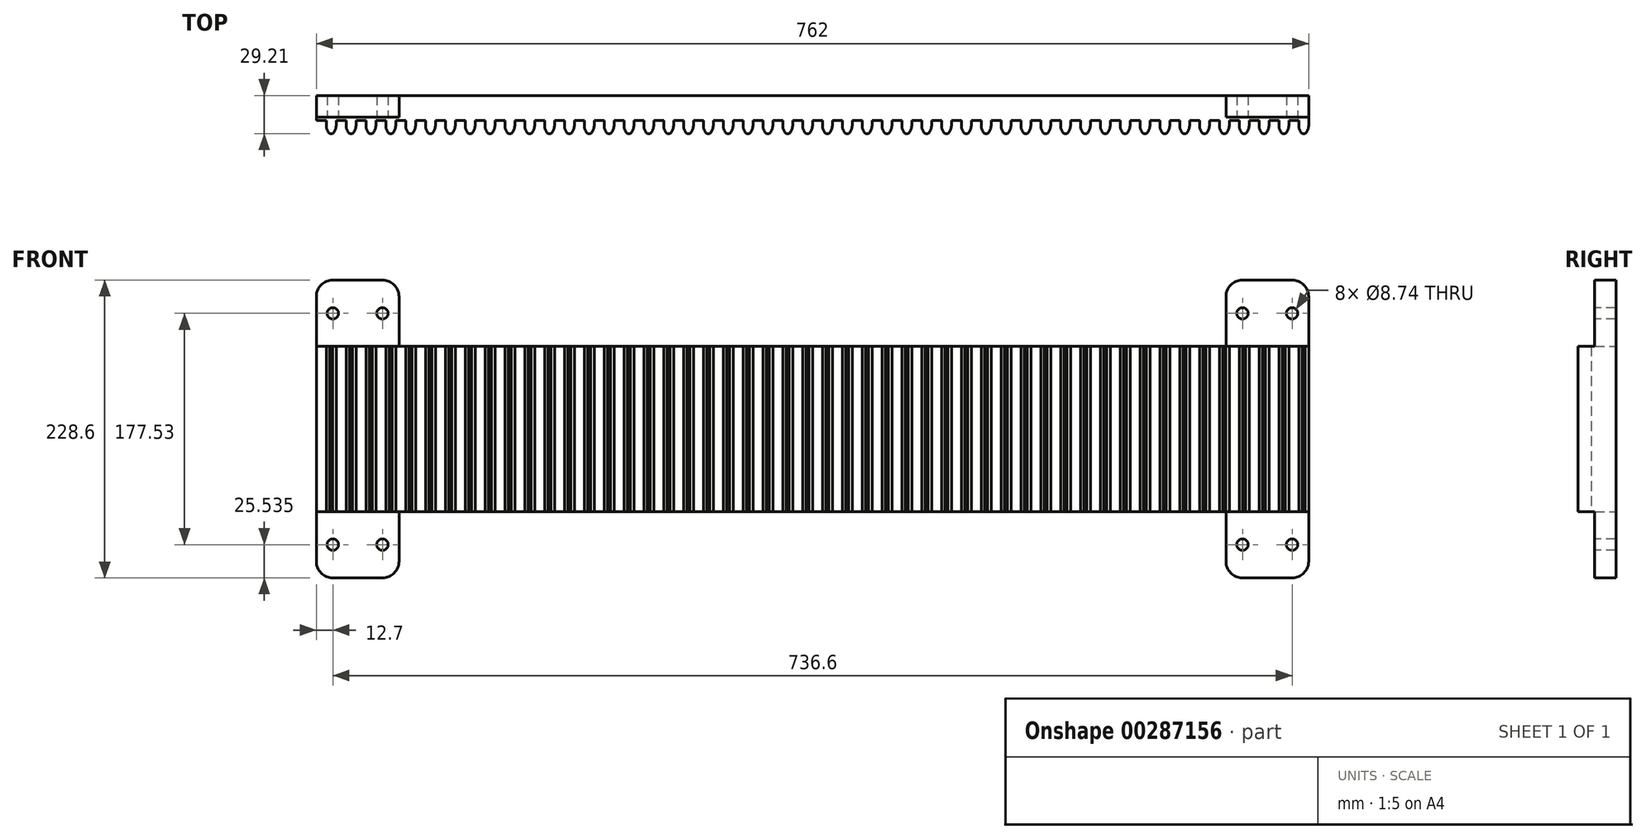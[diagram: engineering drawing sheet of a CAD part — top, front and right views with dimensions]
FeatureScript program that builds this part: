
annotation { "Feature Type Name" : "Feature", "Feature Type Description" : "" }
export const myFeature = defineFeature(function(context is Context, id is Id, definition is map)
    precondition{}
    {
        {
            var Q0;
            Q0=qCreatedBy(makeId("Front.planeOp"),FACE);
            var sketch = newSketch(context, id + "F0", { "sketchPlane" : qUnion([Q0])});
            skLineSegment(sketch, "E0", {"start": v(0, 0) * mm, "end": v(63.5, 0) * mm});
            skLineSegment(sketch, "E1.0", {"start": v(0, 228.6) * mm, "end": v(63.5, 228.6) * mm});
            skLineSegment(sketch, "E2", {"start": v(762, 0) * mm, "end": v(762, 228.6) * mm});
            skLineSegment(sketch, "E3", {"start": v(0, 228.6) * mm, "end": v(0, 0) * mm});
            skLineSegment(sketch, "E4.0", {"start": v(63.5, 177.8) * mm, "end": v(698.5, 177.8) * mm});
            skLineSegment(sketch, "E5.0", {"start": v(63.5, 50.8) * mm, "end": v(698.5, 50.8) * mm});
            skLineSegment(sketch, "E6.0", {"start": v(63.5, 228.6) * mm, "end": v(63.5, 177.8) * mm});
            skLineSegment(sketch, "E7.0", {"start": v(698.5, 0) * mm, "end": v(698.5, 50.8) * mm});
            skLineSegment(sketch, "E8.trimOffspring", {"start": v(698.5, 228.6) * mm, "end": v(762, 228.6) * mm});
            skLineSegment(sketch, "E9.trimOffspring", {"start": v(698.5, 0) * mm, "end": v(762, 0) * mm});
            skLineSegment(sketch, "E10.trimOffspring", {"start": v(698.5, 177.8) * mm, "end": v(698.5, 228.6) * mm});
            skLineSegment(sketch, "E11.trimOffspring", {"start": v(63.5, 50.8) * mm, "end": v(63.5, 0) * mm});
            skSolve(sketch);
        }
        {
            var Q0;
            Q0=qSketchRegion(id+"F0",true);
            extrude(context, id + "F1", {"entities" : qUnion([Q0]), "depth" : 19.05 * mm});
        }
        {
            var Q0;
            Q0=makeQuery(id+"F1.opExtrude","CAP_FACE",FACE,{"disambiguationData":[OSD([sQuery(id+"F0.wireOp",EDGE,"E0"),sQuery(id+"F0.wireOp",EDGE,"E1.0"),sQuery(id+"F0.wireOp",EDGE,"E2"),sQuery(id+"F0.wireOp",EDGE,"E3"),sQuery(id+"F0.wireOp",EDGE,"E4.0"),sQuery(id+"F0.wireOp",EDGE,"E5.0"),sQuery(id+"F0.wireOp",EDGE,"E6.0"),sQuery(id+"F0.wireOp",EDGE,"E7.0"),sQuery(id+"F0.wireOp",EDGE,"E8.trimOffspring"),sQuery(id+"F0.wireOp",EDGE,"E9.trimOffspring"),sQuery(id+"F0.wireOp",EDGE,"E10.trimOffspring"),sQuery(id+"F0.wireOp",EDGE,"E11.trimOffspring")])],"isStart":false});
            var sketch = newSketch(context, id + "F2", { "sketchPlane" : qUnion([Q0])});
            skLineSegment(sketch, "E12", {"start": v(762, 177.8) * mm, "end": v(0, 177.8) * mm});
            skLineSegment(sketch, "E13", {"start": v(0, 177.8) * mm, "end": v(0, 50.8) * mm});
            skLineSegment(sketch, "E14", {"start": v(0, 50.8) * mm, "end": v(762, 50.8) * mm});
            skLineSegment(sketch, "E15", {"start": v(762, 50.8) * mm, "end": v(762, 177.8) * mm});
            skLineSegment(sketch, "E16.1.0.0", {"start": v(7.62, 177.8) * mm, "end": v(7.62, 50.8) * mm});
            skLineSegment(sketch, "E16.2.0.0", {"start": v(15.24, 177.8) * mm, "end": v(15.24, 50.8) * mm});
            skLineSegment(sketch, "E16.direction1", {"start": v(0, 50.8) * mm, "end": v(7.62, 50.8) * mm, "construction": true});
            skLineSegment(sketch, "E17.0.3.0", {"start": v(22.86, 177.8) * mm, "end": v(22.86, 50.8) * mm});
            skLineSegment(sketch, "E17.0.4.0", {"start": v(30.48, 177.8) * mm, "end": v(30.48, 50.8) * mm});
            skLineSegment(sketch, "E17.0.5.0", {"start": v(38.1, 177.8) * mm, "end": v(38.1, 50.8) * mm});
            skLineSegment(sketch, "E17.0.6.0", {"start": v(45.72, 177.8) * mm, "end": v(45.72, 50.8) * mm});
            skLineSegment(sketch, "E17.0.7.0", {"start": v(53.34, 177.8) * mm, "end": v(53.34, 50.8) * mm});
            skLineSegment(sketch, "E17.0.8.0", {"start": v(60.96, 177.8) * mm, "end": v(60.96, 50.8) * mm});
            skLineSegment(sketch, "E17.0.9.0", {"start": v(68.58, 177.8) * mm, "end": v(68.58, 50.8) * mm});
            skLineSegment(sketch, "E17.0.10.0", {"start": v(76.2, 177.8) * mm, "end": v(76.2, 50.8) * mm});
            skLineSegment(sketch, "E17.0.11.0", {"start": v(83.82, 177.8) * mm, "end": v(83.82, 50.8) * mm});
            skLineSegment(sketch, "E17.0.12.0", {"start": v(91.44, 177.8) * mm, "end": v(91.44, 50.8) * mm});
            skLineSegment(sketch, "E17.0.13.0", {"start": v(99.06, 177.8) * mm, "end": v(99.06, 50.8) * mm});
            skLineSegment(sketch, "E17.0.14.0", {"start": v(106.68, 177.8) * mm, "end": v(106.68, 50.8) * mm});
            skLineSegment(sketch, "E17.0.15.0", {"start": v(114.3, 177.8) * mm, "end": v(114.3, 50.8) * mm});
            skLineSegment(sketch, "E17.0.16.0", {"start": v(121.92, 177.8) * mm, "end": v(121.92, 50.8) * mm});
            skLineSegment(sketch, "E17.0.17.0", {"start": v(129.54, 177.8) * mm, "end": v(129.54, 50.8) * mm});
            skLineSegment(sketch, "E17.0.18.0", {"start": v(137.16, 177.8) * mm, "end": v(137.16, 50.8) * mm});
            skLineSegment(sketch, "E17.0.19.0", {"start": v(144.78, 177.8) * mm, "end": v(144.78, 50.8) * mm});
            skLineSegment(sketch, "E17.0.20.0", {"start": v(152.4, 177.8) * mm, "end": v(152.4, 50.8) * mm});
            skLineSegment(sketch, "E17.0.21.0", {"start": v(160.02, 177.8) * mm, "end": v(160.02, 50.8) * mm});
            skLineSegment(sketch, "E17.0.22.0", {"start": v(167.64, 177.8) * mm, "end": v(167.64, 50.8) * mm});
            skLineSegment(sketch, "E17.0.23.0", {"start": v(175.26, 177.8) * mm, "end": v(175.26, 50.8) * mm});
            skLineSegment(sketch, "E17.0.24.0", {"start": v(182.88, 177.8) * mm, "end": v(182.88, 50.8) * mm});
            skLineSegment(sketch, "E17.0.25.0", {"start": v(190.5, 177.8) * mm, "end": v(190.5, 50.8) * mm});
            skLineSegment(sketch, "E17.0.26.0", {"start": v(198.12, 177.8) * mm, "end": v(198.12, 50.8) * mm});
            skLineSegment(sketch, "E17.0.27.0", {"start": v(205.74, 177.8) * mm, "end": v(205.74, 50.8) * mm});
            skLineSegment(sketch, "E17.0.28.0", {"start": v(213.36, 177.8) * mm, "end": v(213.36, 50.8) * mm});
            skLineSegment(sketch, "E17.0.29.0", {"start": v(220.98, 177.8) * mm, "end": v(220.98, 50.8) * mm});
            skLineSegment(sketch, "E17.0.30.0", {"start": v(228.6, 177.8) * mm, "end": v(228.6, 50.8) * mm});
            skLineSegment(sketch, "E17.0.31.0", {"start": v(236.22, 177.8) * mm, "end": v(236.22, 50.8) * mm});
            skLineSegment(sketch, "E17.0.32.0", {"start": v(243.84, 177.8) * mm, "end": v(243.84, 50.8) * mm});
            skLineSegment(sketch, "E17.0.33.0", {"start": v(251.46, 177.8) * mm, "end": v(251.46, 50.8) * mm});
            skLineSegment(sketch, "E17.0.34.0", {"start": v(259.08, 177.8) * mm, "end": v(259.08, 50.8) * mm});
            skLineSegment(sketch, "E17.0.35.0", {"start": v(266.7, 177.8) * mm, "end": v(266.7, 50.8) * mm});
            skLineSegment(sketch, "E17.0.36.0", {"start": v(274.32, 177.8) * mm, "end": v(274.32, 50.8) * mm});
            skLineSegment(sketch, "E17.0.37.0", {"start": v(281.94, 177.8) * mm, "end": v(281.94, 50.8) * mm});
            skLineSegment(sketch, "E17.0.38.0", {"start": v(289.56, 177.8) * mm, "end": v(289.56, 50.8) * mm});
            skLineSegment(sketch, "E17.0.39.0", {"start": v(297.18, 177.8) * mm, "end": v(297.18, 50.8) * mm});
            skLineSegment(sketch, "E17.0.40.0", {"start": v(304.8, 177.8) * mm, "end": v(304.8, 50.8) * mm});
            skLineSegment(sketch, "E17.0.41.0", {"start": v(312.42, 177.8) * mm, "end": v(312.42, 50.8) * mm});
            skLineSegment(sketch, "E17.0.42.0", {"start": v(320.04, 177.8) * mm, "end": v(320.04, 50.8) * mm});
            skLineSegment(sketch, "E17.0.43.0", {"start": v(327.66, 177.8) * mm, "end": v(327.66, 50.8) * mm});
            skLineSegment(sketch, "E17.0.44.0", {"start": v(335.28, 177.8) * mm, "end": v(335.28, 50.8) * mm});
            skLineSegment(sketch, "E17.0.45.0", {"start": v(342.9, 177.8) * mm, "end": v(342.9, 50.8) * mm});
            skLineSegment(sketch, "E17.0.46.0", {"start": v(350.52, 177.8) * mm, "end": v(350.52, 50.8) * mm});
            skLineSegment(sketch, "E17.0.47.0", {"start": v(358.14, 177.8) * mm, "end": v(358.14, 50.8) * mm});
            skLineSegment(sketch, "E17.0.48.0", {"start": v(365.76, 177.8) * mm, "end": v(365.76, 50.8) * mm});
            skLineSegment(sketch, "E17.0.49.0", {"start": v(373.38, 177.8) * mm, "end": v(373.38, 50.8) * mm});
            skLineSegment(sketch, "E18.0.50.0", {"start": v(381, 177.8) * mm, "end": v(381, 50.8) * mm});
            skLineSegment(sketch, "E18.0.51.0", {"start": v(388.62, 177.8) * mm, "end": v(388.62, 50.8) * mm});
            skLineSegment(sketch, "E18.0.52.0", {"start": v(396.24, 177.8) * mm, "end": v(396.24, 50.8) * mm});
            skLineSegment(sketch, "E18.0.53.0", {"start": v(403.86, 177.8) * mm, "end": v(403.86, 50.8) * mm});
            skLineSegment(sketch, "E18.0.54.0", {"start": v(411.48, 177.8) * mm, "end": v(411.48, 50.8) * mm});
            skLineSegment(sketch, "E18.0.55.0", {"start": v(419.1, 177.8) * mm, "end": v(419.1, 50.8) * mm});
            skLineSegment(sketch, "E18.0.56.0", {"start": v(426.72, 177.8) * mm, "end": v(426.72, 50.8) * mm});
            skLineSegment(sketch, "E18.0.57.0", {"start": v(434.34, 177.8) * mm, "end": v(434.34, 50.8) * mm});
            skLineSegment(sketch, "E18.0.58.0", {"start": v(441.96, 177.8) * mm, "end": v(441.96, 50.8) * mm});
            skLineSegment(sketch, "E18.0.59.0", {"start": v(449.58, 177.8) * mm, "end": v(449.58, 50.8) * mm});
            skLineSegment(sketch, "E18.0.60.0", {"start": v(457.2, 177.8) * mm, "end": v(457.2, 50.8) * mm});
            skLineSegment(sketch, "E18.0.61.0", {"start": v(464.82, 177.8) * mm, "end": v(464.82, 50.8) * mm});
            skLineSegment(sketch, "E18.0.62.0", {"start": v(472.44, 177.8) * mm, "end": v(472.44, 50.8) * mm});
            skLineSegment(sketch, "E18.0.63.0", {"start": v(480.06, 177.8) * mm, "end": v(480.06, 50.8) * mm});
            skLineSegment(sketch, "E18.0.64.0", {"start": v(487.68, 177.8) * mm, "end": v(487.68, 50.8) * mm});
            skLineSegment(sketch, "E18.0.65.0", {"start": v(495.3, 177.8) * mm, "end": v(495.3, 50.8) * mm});
            skLineSegment(sketch, "E18.0.66.0", {"start": v(502.92, 177.8) * mm, "end": v(502.92, 50.8) * mm});
            skLineSegment(sketch, "E18.0.67.0", {"start": v(510.54, 177.8) * mm, "end": v(510.54, 50.8) * mm});
            skLineSegment(sketch, "E18.0.68.0", {"start": v(518.16, 177.8) * mm, "end": v(518.16, 50.8) * mm});
            skLineSegment(sketch, "E18.0.69.0", {"start": v(525.78, 177.8) * mm, "end": v(525.78, 50.8) * mm});
            skLineSegment(sketch, "E18.0.70.0", {"start": v(533.4, 177.8) * mm, "end": v(533.4, 50.8) * mm});
            skLineSegment(sketch, "E18.0.71.0", {"start": v(541.02, 177.8) * mm, "end": v(541.02, 50.8) * mm});
            skLineSegment(sketch, "E18.0.72.0", {"start": v(548.64, 177.8) * mm, "end": v(548.64, 50.8) * mm});
            skLineSegment(sketch, "E18.0.73.0", {"start": v(556.26, 177.8) * mm, "end": v(556.26, 50.8) * mm});
            skLineSegment(sketch, "E18.0.74.0", {"start": v(563.88, 177.8) * mm, "end": v(563.88, 50.8) * mm});
            skLineSegment(sketch, "E18.0.75.0", {"start": v(571.5, 177.8) * mm, "end": v(571.5, 50.8) * mm});
            skLineSegment(sketch, "E18.0.76.0", {"start": v(579.12, 177.8) * mm, "end": v(579.12, 50.8) * mm});
            skLineSegment(sketch, "E18.0.77.0", {"start": v(586.74, 177.8) * mm, "end": v(586.74, 50.8) * mm});
            skLineSegment(sketch, "E18.0.78.0", {"start": v(594.36, 177.8) * mm, "end": v(594.36, 50.8) * mm});
            skLineSegment(sketch, "E18.0.79.0", {"start": v(601.98, 177.8) * mm, "end": v(601.98, 50.8) * mm});
            skLineSegment(sketch, "E18.0.80.0", {"start": v(609.6, 177.8) * mm, "end": v(609.6, 50.8) * mm});
            skLineSegment(sketch, "E18.0.81.0", {"start": v(617.22, 177.8) * mm, "end": v(617.22, 50.8) * mm});
            skLineSegment(sketch, "E18.0.82.0", {"start": v(624.84, 177.8) * mm, "end": v(624.84, 50.8) * mm});
            skLineSegment(sketch, "E18.0.83.0", {"start": v(632.46, 177.8) * mm, "end": v(632.46, 50.8) * mm});
            skLineSegment(sketch, "E18.0.84.0", {"start": v(640.08, 177.8) * mm, "end": v(640.08, 50.8) * mm});
            skLineSegment(sketch, "E18.0.85.0", {"start": v(647.7, 177.8) * mm, "end": v(647.7, 50.8) * mm});
            skLineSegment(sketch, "E18.0.86.0", {"start": v(655.32, 177.8) * mm, "end": v(655.32, 50.8) * mm});
            skLineSegment(sketch, "E18.0.87.0", {"start": v(662.94, 177.8) * mm, "end": v(662.94, 50.8) * mm});
            skLineSegment(sketch, "E18.0.88.0", {"start": v(670.56, 177.8) * mm, "end": v(670.56, 50.8) * mm});
            skLineSegment(sketch, "E18.0.89.0", {"start": v(678.18, 177.8) * mm, "end": v(678.18, 50.8) * mm});
            skLineSegment(sketch, "E18.0.90.0", {"start": v(685.8, 177.8) * mm, "end": v(685.8, 50.8) * mm});
            skLineSegment(sketch, "E18.0.91.0", {"start": v(693.42, 177.8) * mm, "end": v(693.42, 50.8) * mm});
            skLineSegment(sketch, "E18.0.92.0", {"start": v(701.04, 177.8) * mm, "end": v(701.04, 50.8) * mm});
            skLineSegment(sketch, "E18.0.93.0", {"start": v(708.66, 177.8) * mm, "end": v(708.66, 50.8) * mm});
            skLineSegment(sketch, "E18.0.94.0", {"start": v(716.28, 177.8) * mm, "end": v(716.28, 50.8) * mm});
            skLineSegment(sketch, "E18.0.95.0", {"start": v(723.9, 177.8) * mm, "end": v(723.9, 50.8) * mm});
            skLineSegment(sketch, "E18.0.96.0", {"start": v(731.52, 177.8) * mm, "end": v(731.52, 50.8) * mm});
            skLineSegment(sketch, "E18.0.97.0", {"start": v(739.14, 177.8) * mm, "end": v(739.14, 50.8) * mm});
            skLineSegment(sketch, "E18.0.98.0", {"start": v(746.76, 177.8) * mm, "end": v(746.76, 50.8) * mm});
            skLineSegment(sketch, "E18.0.99.0", {"start": v(754.38, 177.8) * mm, "end": v(754.38, 50.8) * mm});
            skSolve(sketch);
        }
        {
            var Q0;
            {var subQ7=makeQuery(id+"F1.opExtrude","CAP_EDGE",EDGE,{"disambiguationData":[OSD([sQuery(id+"F0.wireOp",EDGE,"E1.0")])],"isStart":false});Q0=makeQuery(id+"F2.imprint","IMPRINT",FACE,{"disambiguationData":[TD([[makeQuery(id+"F2.imprint","IMPRINT",EDGE,{"derivedFrom":subQ7}),-1.0]])]});}
            var sketch = newSketch(context, id + "F3", { "sketchPlane" : qUnion([Q0])});
            skLineSegment(sketch, "E19", {"start": v(0, 228.6) * mm, "end": v(63.5, 228.6) * mm});
            skLineSegment(sketch, "E20", {"start": v(63.5, 228.6) * mm, "end": v(63.5, 177.8) * mm});
            skLineSegment(sketch, "E21", {"start": v(63.5, 177.8) * mm, "end": v(0, 177.8) * mm});
            skLineSegment(sketch, "E22", {"start": v(0, 0) * mm, "end": v(0, 50.8) * mm});
            skLineSegment(sketch, "E23", {"start": v(0, 50.8) * mm, "end": v(63.5, 50.8) * mm});
            skLineSegment(sketch, "E24", {"start": v(63.5, 50.8) * mm, "end": v(63.5, 0) * mm});
            skLineSegment(sketch, "E25", {"start": v(63.5, 0) * mm, "end": v(0, 0) * mm});
            skSolve(sketch);
        }
        {
            var Q0;
            Q0=qSketchRegion(id+"F3",true);
            var Q1;
            {var subQ8=sQuery(id+"F3.wireOp",EDGE,"E19");Q1=makeQuery(id+"F3.imprint","IMPRINT",FACE,{"disambiguationData":[TD([[makeQuery(id+"F3.imprint","IMPRINT",EDGE,{"derivedFrom":subQ8}),-1.0]])]});}
            extrude(context, id + "F4", {"entities" : qUnion([Q0, Q1]), "operationType" : NewBodyOperationType.REMOVE, "oppositeDirection" : true, "depth" : 2.54 * mm});
        }
        {
            var Q0;
            {var subQ1=sQuery(id+"F0.wireOp",EDGE,"E7.0");var subQ7=sQuery(id+"F0.wireOp",EDGE,"E8.trimOffspring");var subQ10=sQuery(id+"F0.wireOp",EDGE,"E9.trimOffspring");var subQ50=sQuery(id+"F0.wireOp",EDGE,"E4.0");var subQ83=sQuery(id+"F0.wireOp",EDGE,"E10.trimOffspring");var subQ89=sQuery(id+"F0.wireOp",EDGE,"E2");var subQ94=sQuery(id+"F0.wireOp",EDGE,"E5.0");Q0=makeQuery(id+"F9L2YdqkWQCteiL_1.boolean.opBoolean","SPLIT",FACE,{"disambiguationData":[TD([makeQuery(id+"F1.opExtrude","SWEPT_FACE",FACE,{"disambiguationData":[OSD([subQ89])]})])],"derivedFrom":makeQuery(id+"F1.opExtrude","CAP_FACE",FACE,{"disambiguationData":[OSD([sQuery(id+"F0.wireOp",EDGE,"E0"),sQuery(id+"F0.wireOp",EDGE,"E1.0"),subQ89,sQuery(id+"F0.wireOp",EDGE,"E3"),subQ50,subQ94,sQuery(id+"F0.wireOp",EDGE,"E6.0"),subQ1,subQ7,subQ10,subQ83,sQuery(id+"F0.wireOp",EDGE,"E11.trimOffspring")])],"isStart":false})});}
            var sketch = newSketch(context, id + "F5", { "sketchPlane" : qUnion([Q0])});
            skLineSegment(sketch, "E26", {"start": v(698.5, 228.6) * mm, "end": v(698.5, 177.8) * mm});
            skLineSegment(sketch, "E27", {"start": v(698.5, 177.8) * mm, "end": v(762, 177.8) * mm});
            skLineSegment(sketch, "E28", {"start": v(762, 177.8) * mm, "end": v(762, 228.6) * mm});
            skLineSegment(sketch, "E29", {"start": v(762, 228.6) * mm, "end": v(698.5, 228.6) * mm});
            skLineSegment(sketch, "E30", {"start": v(698.5, 0) * mm, "end": v(762, 0) * mm});
            skLineSegment(sketch, "E31", {"start": v(762, 0) * mm, "end": v(762, 50.8) * mm});
            skLineSegment(sketch, "E32", {"start": v(762, 50.8) * mm, "end": v(701.04, 50.8) * mm});
            skLineSegment(sketch, "E33", {"start": v(701.04, 50.8) * mm, "end": v(698.5, 50.8) * mm});
            skLineSegment(sketch, "E34", {"start": v(698.5, 50.8) * mm, "end": v(698.5, 0) * mm});
            skSolve(sketch);
        }
        {
            var Q0;
            {var subQ7=sQuery(id+"F5.wireOp",EDGE,"E26");Q0=makeQuery(id+"F5.imprint","IMPRINT",FACE,{"disambiguationData":[TD([[makeQuery(id+"F5.imprint","IMPRINT",EDGE,{"derivedFrom":subQ7}),-1.0]])]});}
            var Q1;
            Q1=makeQuery(id+"F5.imprint","IMPRINT",FACE,{"disambiguationData":[TD([[makeQuery(id+"F5.imprint","IMPRINT",EDGE,{"derivedFrom":sQuery(id+"F5.wireOp",EDGE,"E30")}),1.0]])]});
            extrude(context, id + "F6", {"entities" : qUnion([Q0, Q1]), "operationType" : NewBodyOperationType.REMOVE, "oppositeDirection" : true, "depth" : 2.54 * mm});
        }
        {
            var Q0;
            Q0=makeQuery(id+"F1.opExtrude","SWEPT_EDGE",EDGE,{"disambiguationData":[OSD([sQuery(id+"F0.wireOp",EDGE,"E1.0"),sQuery(id+"F0.wireOp",EDGE,"E6.0")])]});
            var Q1;
            Q1=makeQuery(id+"F1.opExtrude","SWEPT_EDGE",EDGE,{"disambiguationData":[OSD([sQuery(id+"F0.wireOp",EDGE,"E1.0"),sQuery(id+"F0.wireOp",EDGE,"E3")])]});
            var Q2;
            Q2=makeQuery(id+"F1.opExtrude","SWEPT_EDGE",EDGE,{"disambiguationData":[OSD([sQuery(id+"F0.wireOp",EDGE,"E0"),sQuery(id+"F0.wireOp",EDGE,"E11.trimOffspring")])]});
            var Q3;
            Q3=makeQuery(id+"F1.opExtrude","SWEPT_EDGE",EDGE,{"disambiguationData":[OSD([sQuery(id+"F0.wireOp",EDGE,"E0"),sQuery(id+"F0.wireOp",EDGE,"E3")])]});
            var Q4;
            Q4=makeQuery(id+"F1.opExtrude","SWEPT_EDGE",EDGE,{"disambiguationData":[OSD([sQuery(id+"F0.wireOp",EDGE,"E2"),sQuery(id+"F0.wireOp",EDGE,"E8.trimOffspring")])]});
            var Q5;
            Q5=makeQuery(id+"F1.opExtrude","SWEPT_EDGE",EDGE,{"disambiguationData":[OSD([sQuery(id+"F0.wireOp",EDGE,"E8.trimOffspring"),sQuery(id+"F0.wireOp",EDGE,"E10.trimOffspring")])]});
            var Q6;
            Q6=makeQuery(id+"F1.opExtrude","SWEPT_EDGE",EDGE,{"disambiguationData":[OSD([sQuery(id+"F0.wireOp",EDGE,"E2"),sQuery(id+"F0.wireOp",EDGE,"E9.trimOffspring")])]});
            var Q7;
            Q7=makeQuery(id+"F1.opExtrude","SWEPT_EDGE",EDGE,{"disambiguationData":[OSD([sQuery(id+"F0.wireOp",EDGE,"E7.0"),sQuery(id+"F0.wireOp",EDGE,"E9.trimOffspring")])]});
            fillet(context, id + "F7", {"entities" : qUnion([Q0, Q1, Q2, Q3, Q4, Q5, Q6, Q7]), "radius" : 12.7 * mm, "tangentPropagation" : true, "allowEdgeOverflow" : false});
        }
        {
            var Q0;
            {var subQ0=sQuery(id+"F2.wireOp",EDGE,"E14");var subQ1=makeQuery(id+"F2.imprint","INTERSECT",VERTEX,{"derivedFrom":[makeQuery(id+"F1.opExtrude","CAP_EDGE",EDGE,{"disambiguationData":[OSD([sQuery(id+"F0.wireOp",EDGE,"E7.0")])],"isStart":false}),subQ0]});Q0=makeQuery(id+"F6.boolean.opBoolean","MERGE",FACE,{"derivedFrom":[makeQuery(id+"F9L2YdqkWQCteiL_1.opExtrude","SWEPT_FACE",FACE,{"disambiguationData":[OSD([subQ0]),TDD([makeQuery(id+"F2.imprint","IMPRINT",EDGE,{"disambiguationData":[TD([[makeQuery(id+"F2.imprint","INTERSECT",VERTEX,{"derivedFrom":[subQ0,sQuery(id+"F2.wireOp",EDGE,"E18.0.93.0")]}),-1.0]])],"derivedFrom":subQ0})])]}),makeQuery(id+"F9L2YdqkWQCteiL_1.opExtrude","SWEPT_FACE",FACE,{"disambiguationData":[OSD([subQ0]),TDD([makeQuery(id+"F2.imprint","IMPRINT",EDGE,{"disambiguationData":[TD([[makeQuery(id+"F2.imprint","INTERSECT",VERTEX,{"derivedFrom":[subQ0,sQuery(id+"F2.wireOp",EDGE,"E18.0.95.0")]}),-1.0]])],"derivedFrom":subQ0})])]}),makeQuery(id+"F9L2YdqkWQCteiL_1.opExtrude","SWEPT_FACE",FACE,{"disambiguationData":[OSD([subQ0]),TDD([makeQuery(id+"F2.imprint","IMPRINT",EDGE,{"disambiguationData":[TD([[makeQuery(id+"F2.imprint","INTERSECT",VERTEX,{"derivedFrom":[subQ0,sQuery(id+"F2.wireOp",EDGE,"E18.0.97.0")]}),-1.0]])],"derivedFrom":subQ0})])]}),makeQuery(id+"F9L2YdqkWQCteiL_1.opExtrude","SWEPT_FACE",FACE,{"disambiguationData":[OSD([subQ0]),TDD([makeQuery(id+"F2.imprint","IMPRINT",EDGE,{"disambiguationData":[TD([[makeQuery(id+"F2.imprint","INTERSECT",VERTEX,{"derivedFrom":[subQ0,sQuery(id+"F2.wireOp",EDGE,"E18.0.99.0")]}),-1.0]])],"derivedFrom":subQ0})])]}),makeQuery(id+"F4.boolean.opBoolean","MERGE",FACE,{"derivedFrom":[makeQuery(id+"F9L2YdqkWQCteiL_1.opExtrude","SWEPT_FACE",FACE,{"disambiguationData":[OSD([subQ0]),TDD([makeQuery(id+"F2.imprint","IMPRINT",EDGE,{"disambiguationData":[TD([[makeQuery(id+"F2.imprint","INTERSECT",VERTEX,{"derivedFrom":[subQ0,sQuery(id+"F2.wireOp",EDGE,"E16.1.0.0")]}),-1.0]])],"derivedFrom":subQ0})])]}),makeQuery(id+"F9L2YdqkWQCteiL_1.opExtrude","SWEPT_FACE",FACE,{"disambiguationData":[OSD([subQ0]),TDD([makeQuery(id+"F2.imprint","IMPRINT",EDGE,{"disambiguationData":[TD([[makeQuery(id+"F2.imprint","INTERSECT",VERTEX,{"derivedFrom":[subQ0,sQuery(id+"F2.wireOp",EDGE,"E17.0.3.0")]}),-1.0]])],"derivedFrom":subQ0})])]}),makeQuery(id+"F9L2YdqkWQCteiL_1.opExtrude","SWEPT_FACE",FACE,{"disambiguationData":[OSD([subQ0]),TDD([makeQuery(id+"F2.imprint","IMPRINT",EDGE,{"disambiguationData":[TD([[makeQuery(id+"F2.imprint","INTERSECT",VERTEX,{"derivedFrom":[subQ0,sQuery(id+"F2.wireOp",EDGE,"E17.0.5.0")]}),-1.0]])],"derivedFrom":subQ0})])]}),makeQuery(id+"F9L2YdqkWQCteiL_1.opExtrude","SWEPT_FACE",FACE,{"disambiguationData":[OSD([subQ0]),TDD([makeQuery(id+"F2.imprint","IMPRINT",EDGE,{"disambiguationData":[TD([[makeQuery(id+"F2.imprint","INTERSECT",VERTEX,{"derivedFrom":[subQ0,sQuery(id+"F2.wireOp",EDGE,"E17.0.7.0")]}),-1.0]])],"derivedFrom":subQ0})])]}),makeQuery(id+"F9L2YdqkWQCteiL_1.boolean.opBoolean","MERGE",FACE,{"derivedFrom":[makeQuery(id+"F1.opExtrude","SWEPT_FACE",FACE,{"disambiguationData":[OSD([sQuery(id+"F0.wireOp",EDGE,"E5.0")])]}),makeQuery(id+"F9L2YdqkWQCteiL_1.opExtrude","SWEPT_FACE",FACE,{"disambiguationData":[OSD([subQ0]),TDD([makeQuery(id+"F2.imprint","IMPRINT",EDGE,{"disambiguationData":[TD([[makeQuery(id+"F2.imprint","INTERSECT",VERTEX,{"derivedFrom":[subQ0,sQuery(id+"F2.wireOp",EDGE,"E17.0.9.0")]}),-1.0]])],"derivedFrom":subQ0})])]}),makeQuery(id+"F9L2YdqkWQCteiL_1.opExtrude","SWEPT_FACE",FACE,{"disambiguationData":[OSD([subQ0]),TDD([makeQuery(id+"F2.imprint","IMPRINT",EDGE,{"disambiguationData":[TD([[makeQuery(id+"F2.imprint","INTERSECT",VERTEX,{"derivedFrom":[subQ0,sQuery(id+"F2.wireOp",EDGE,"E17.0.11.0")]}),-1.0]])],"derivedFrom":subQ0})])]}),makeQuery(id+"F9L2YdqkWQCteiL_1.opExtrude","SWEPT_FACE",FACE,{"disambiguationData":[OSD([subQ0]),TDD([makeQuery(id+"F2.imprint","IMPRINT",EDGE,{"disambiguationData":[TD([[makeQuery(id+"F2.imprint","INTERSECT",VERTEX,{"derivedFrom":[subQ0,sQuery(id+"F2.wireOp",EDGE,"E17.0.13.0")]}),-1.0]])],"derivedFrom":subQ0})])]}),makeQuery(id+"F9L2YdqkWQCteiL_1.opExtrude","SWEPT_FACE",FACE,{"disambiguationData":[OSD([subQ0]),TDD([makeQuery(id+"F2.imprint","IMPRINT",EDGE,{"disambiguationData":[TD([[makeQuery(id+"F2.imprint","INTERSECT",VERTEX,{"derivedFrom":[subQ0,sQuery(id+"F2.wireOp",EDGE,"E17.0.15.0")]}),-1.0]])],"derivedFrom":subQ0})])]}),makeQuery(id+"F9L2YdqkWQCteiL_1.opExtrude","SWEPT_FACE",FACE,{"disambiguationData":[OSD([subQ0]),TDD([makeQuery(id+"F2.imprint","IMPRINT",EDGE,{"disambiguationData":[TD([[makeQuery(id+"F2.imprint","INTERSECT",VERTEX,{"derivedFrom":[subQ0,sQuery(id+"F2.wireOp",EDGE,"E17.0.17.0")]}),-1.0]])],"derivedFrom":subQ0})])]}),makeQuery(id+"F9L2YdqkWQCteiL_1.opExtrude","SWEPT_FACE",FACE,{"disambiguationData":[OSD([subQ0]),TDD([makeQuery(id+"F2.imprint","IMPRINT",EDGE,{"disambiguationData":[TD([[makeQuery(id+"F2.imprint","INTERSECT",VERTEX,{"derivedFrom":[subQ0,sQuery(id+"F2.wireOp",EDGE,"E17.0.19.0")]}),-1.0]])],"derivedFrom":subQ0})])]}),makeQuery(id+"F9L2YdqkWQCteiL_1.opExtrude","SWEPT_FACE",FACE,{"disambiguationData":[OSD([subQ0]),TDD([makeQuery(id+"F2.imprint","IMPRINT",EDGE,{"disambiguationData":[TD([[makeQuery(id+"F2.imprint","INTERSECT",VERTEX,{"derivedFrom":[subQ0,sQuery(id+"F2.wireOp",EDGE,"E17.0.21.0")]}),-1.0]])],"derivedFrom":subQ0})])]}),makeQuery(id+"F9L2YdqkWQCteiL_1.opExtrude","SWEPT_FACE",FACE,{"disambiguationData":[OSD([subQ0]),TDD([makeQuery(id+"F2.imprint","IMPRINT",EDGE,{"disambiguationData":[TD([[makeQuery(id+"F2.imprint","INTERSECT",VERTEX,{"derivedFrom":[subQ0,sQuery(id+"F2.wireOp",EDGE,"E17.0.23.0")]}),-1.0]])],"derivedFrom":subQ0})])]}),makeQuery(id+"F9L2YdqkWQCteiL_1.opExtrude","SWEPT_FACE",FACE,{"disambiguationData":[OSD([subQ0]),TDD([makeQuery(id+"F2.imprint","IMPRINT",EDGE,{"disambiguationData":[TD([[makeQuery(id+"F2.imprint","INTERSECT",VERTEX,{"derivedFrom":[subQ0,sQuery(id+"F2.wireOp",EDGE,"E17.0.25.0")]}),-1.0]])],"derivedFrom":subQ0})])]}),makeQuery(id+"F9L2YdqkWQCteiL_1.opExtrude","SWEPT_FACE",FACE,{"disambiguationData":[OSD([subQ0]),TDD([makeQuery(id+"F2.imprint","IMPRINT",EDGE,{"disambiguationData":[TD([[makeQuery(id+"F2.imprint","INTERSECT",VERTEX,{"derivedFrom":[subQ0,sQuery(id+"F2.wireOp",EDGE,"E17.0.27.0")]}),-1.0]])],"derivedFrom":subQ0})])]}),makeQuery(id+"F9L2YdqkWQCteiL_1.opExtrude","SWEPT_FACE",FACE,{"disambiguationData":[OSD([subQ0]),TDD([makeQuery(id+"F2.imprint","IMPRINT",EDGE,{"disambiguationData":[TD([[makeQuery(id+"F2.imprint","INTERSECT",VERTEX,{"derivedFrom":[subQ0,sQuery(id+"F2.wireOp",EDGE,"E17.0.29.0")]}),-1.0]])],"derivedFrom":subQ0})])]}),makeQuery(id+"F9L2YdqkWQCteiL_1.opExtrude","SWEPT_FACE",FACE,{"disambiguationData":[OSD([subQ0]),TDD([makeQuery(id+"F2.imprint","IMPRINT",EDGE,{"disambiguationData":[TD([[makeQuery(id+"F2.imprint","INTERSECT",VERTEX,{"derivedFrom":[subQ0,sQuery(id+"F2.wireOp",EDGE,"E17.0.31.0")]}),-1.0]])],"derivedFrom":subQ0})])]}),makeQuery(id+"F9L2YdqkWQCteiL_1.opExtrude","SWEPT_FACE",FACE,{"disambiguationData":[OSD([subQ0]),TDD([makeQuery(id+"F2.imprint","IMPRINT",EDGE,{"disambiguationData":[TD([[makeQuery(id+"F2.imprint","INTERSECT",VERTEX,{"derivedFrom":[subQ0,sQuery(id+"F2.wireOp",EDGE,"E17.0.33.0")]}),-1.0]])],"derivedFrom":subQ0})])]}),makeQuery(id+"F9L2YdqkWQCteiL_1.opExtrude","SWEPT_FACE",FACE,{"disambiguationData":[OSD([subQ0]),TDD([makeQuery(id+"F2.imprint","IMPRINT",EDGE,{"disambiguationData":[TD([[makeQuery(id+"F2.imprint","INTERSECT",VERTEX,{"derivedFrom":[subQ0,sQuery(id+"F2.wireOp",EDGE,"E17.0.35.0")]}),-1.0]])],"derivedFrom":subQ0})])]}),makeQuery(id+"F9L2YdqkWQCteiL_1.opExtrude","SWEPT_FACE",FACE,{"disambiguationData":[OSD([subQ0]),TDD([makeQuery(id+"F2.imprint","IMPRINT",EDGE,{"disambiguationData":[TD([[makeQuery(id+"F2.imprint","INTERSECT",VERTEX,{"derivedFrom":[subQ0,sQuery(id+"F2.wireOp",EDGE,"E17.0.37.0")]}),-1.0]])],"derivedFrom":subQ0})])]}),makeQuery(id+"F9L2YdqkWQCteiL_1.opExtrude","SWEPT_FACE",FACE,{"disambiguationData":[OSD([subQ0]),TDD([makeQuery(id+"F2.imprint","IMPRINT",EDGE,{"disambiguationData":[TD([[makeQuery(id+"F2.imprint","INTERSECT",VERTEX,{"derivedFrom":[subQ0,sQuery(id+"F2.wireOp",EDGE,"E17.0.39.0")]}),-1.0]])],"derivedFrom":subQ0})])]}),makeQuery(id+"F9L2YdqkWQCteiL_1.opExtrude","SWEPT_FACE",FACE,{"disambiguationData":[OSD([subQ0]),TDD([makeQuery(id+"F2.imprint","IMPRINT",EDGE,{"disambiguationData":[TD([[makeQuery(id+"F2.imprint","INTERSECT",VERTEX,{"derivedFrom":[subQ0,sQuery(id+"F2.wireOp",EDGE,"E17.0.41.0")]}),-1.0]])],"derivedFrom":subQ0})])]}),makeQuery(id+"F9L2YdqkWQCteiL_1.opExtrude","SWEPT_FACE",FACE,{"disambiguationData":[OSD([subQ0]),TDD([makeQuery(id+"F2.imprint","IMPRINT",EDGE,{"disambiguationData":[TD([[makeQuery(id+"F2.imprint","INTERSECT",VERTEX,{"derivedFrom":[subQ0,sQuery(id+"F2.wireOp",EDGE,"E17.0.43.0")]}),-1.0]])],"derivedFrom":subQ0})])]}),makeQuery(id+"F9L2YdqkWQCteiL_1.opExtrude","SWEPT_FACE",FACE,{"disambiguationData":[OSD([subQ0]),TDD([makeQuery(id+"F2.imprint","IMPRINT",EDGE,{"disambiguationData":[TD([[makeQuery(id+"F2.imprint","INTERSECT",VERTEX,{"derivedFrom":[subQ0,sQuery(id+"F2.wireOp",EDGE,"E17.0.45.0")]}),-1.0]])],"derivedFrom":subQ0})])]}),makeQuery(id+"F9L2YdqkWQCteiL_1.opExtrude","SWEPT_FACE",FACE,{"disambiguationData":[OSD([subQ0]),TDD([makeQuery(id+"F2.imprint","IMPRINT",EDGE,{"disambiguationData":[TD([[makeQuery(id+"F2.imprint","INTERSECT",VERTEX,{"derivedFrom":[subQ0,sQuery(id+"F2.wireOp",EDGE,"E17.0.47.0")]}),-1.0]])],"derivedFrom":subQ0})])]}),makeQuery(id+"F9L2YdqkWQCteiL_1.opExtrude","SWEPT_FACE",FACE,{"disambiguationData":[OSD([subQ0]),TDD([makeQuery(id+"F2.imprint","IMPRINT",EDGE,{"disambiguationData":[TD([[makeQuery(id+"F2.imprint","INTERSECT",VERTEX,{"derivedFrom":[subQ0,sQuery(id+"F2.wireOp",EDGE,"E17.0.49.0")]}),-1.0]])],"derivedFrom":subQ0})])]}),makeQuery(id+"F9L2YdqkWQCteiL_1.opExtrude","SWEPT_FACE",FACE,{"disambiguationData":[OSD([subQ0]),TDD([makeQuery(id+"F2.imprint","IMPRINT",EDGE,{"disambiguationData":[TD([[makeQuery(id+"F2.imprint","INTERSECT",VERTEX,{"derivedFrom":[subQ0,sQuery(id+"F2.wireOp",EDGE,"E18.0.51.0")]}),-1.0]])],"derivedFrom":subQ0})])]}),makeQuery(id+"F9L2YdqkWQCteiL_1.opExtrude","SWEPT_FACE",FACE,{"disambiguationData":[OSD([subQ0]),TDD([makeQuery(id+"F2.imprint","IMPRINT",EDGE,{"disambiguationData":[TD([[makeQuery(id+"F2.imprint","INTERSECT",VERTEX,{"derivedFrom":[subQ0,sQuery(id+"F2.wireOp",EDGE,"E18.0.53.0")]}),-1.0]])],"derivedFrom":subQ0})])]}),makeQuery(id+"F9L2YdqkWQCteiL_1.opExtrude","SWEPT_FACE",FACE,{"disambiguationData":[OSD([subQ0]),TDD([makeQuery(id+"F2.imprint","IMPRINT",EDGE,{"disambiguationData":[TD([[makeQuery(id+"F2.imprint","INTERSECT",VERTEX,{"derivedFrom":[subQ0,sQuery(id+"F2.wireOp",EDGE,"E18.0.55.0")]}),-1.0]])],"derivedFrom":subQ0})])]}),makeQuery(id+"F9L2YdqkWQCteiL_1.opExtrude","SWEPT_FACE",FACE,{"disambiguationData":[OSD([subQ0]),TDD([makeQuery(id+"F2.imprint","IMPRINT",EDGE,{"disambiguationData":[TD([[makeQuery(id+"F2.imprint","INTERSECT",VERTEX,{"derivedFrom":[subQ0,sQuery(id+"F2.wireOp",EDGE,"E18.0.57.0")]}),-1.0]])],"derivedFrom":subQ0})])]}),makeQuery(id+"F9L2YdqkWQCteiL_1.opExtrude","SWEPT_FACE",FACE,{"disambiguationData":[OSD([subQ0]),TDD([makeQuery(id+"F2.imprint","IMPRINT",EDGE,{"disambiguationData":[TD([[makeQuery(id+"F2.imprint","INTERSECT",VERTEX,{"derivedFrom":[subQ0,sQuery(id+"F2.wireOp",EDGE,"E18.0.59.0")]}),-1.0]])],"derivedFrom":subQ0})])]}),makeQuery(id+"F9L2YdqkWQCteiL_1.opExtrude","SWEPT_FACE",FACE,{"disambiguationData":[OSD([subQ0]),TDD([makeQuery(id+"F2.imprint","IMPRINT",EDGE,{"disambiguationData":[TD([[makeQuery(id+"F2.imprint","INTERSECT",VERTEX,{"derivedFrom":[subQ0,sQuery(id+"F2.wireOp",EDGE,"E18.0.61.0")]}),-1.0]])],"derivedFrom":subQ0})])]}),makeQuery(id+"F9L2YdqkWQCteiL_1.opExtrude","SWEPT_FACE",FACE,{"disambiguationData":[OSD([subQ0]),TDD([makeQuery(id+"F2.imprint","IMPRINT",EDGE,{"disambiguationData":[TD([[makeQuery(id+"F2.imprint","INTERSECT",VERTEX,{"derivedFrom":[subQ0,sQuery(id+"F2.wireOp",EDGE,"E18.0.63.0")]}),-1.0]])],"derivedFrom":subQ0})])]}),makeQuery(id+"F9L2YdqkWQCteiL_1.opExtrude","SWEPT_FACE",FACE,{"disambiguationData":[OSD([subQ0]),TDD([makeQuery(id+"F2.imprint","IMPRINT",EDGE,{"disambiguationData":[TD([[makeQuery(id+"F2.imprint","INTERSECT",VERTEX,{"derivedFrom":[subQ0,sQuery(id+"F2.wireOp",EDGE,"E18.0.65.0")]}),-1.0]])],"derivedFrom":subQ0})])]}),makeQuery(id+"F9L2YdqkWQCteiL_1.opExtrude","SWEPT_FACE",FACE,{"disambiguationData":[OSD([subQ0]),TDD([makeQuery(id+"F2.imprint","IMPRINT",EDGE,{"disambiguationData":[TD([[makeQuery(id+"F2.imprint","INTERSECT",VERTEX,{"derivedFrom":[subQ0,sQuery(id+"F2.wireOp",EDGE,"E18.0.67.0")]}),-1.0]])],"derivedFrom":subQ0})])]}),makeQuery(id+"F9L2YdqkWQCteiL_1.opExtrude","SWEPT_FACE",FACE,{"disambiguationData":[OSD([subQ0]),TDD([makeQuery(id+"F2.imprint","IMPRINT",EDGE,{"disambiguationData":[TD([[makeQuery(id+"F2.imprint","INTERSECT",VERTEX,{"derivedFrom":[subQ0,sQuery(id+"F2.wireOp",EDGE,"E18.0.69.0")]}),-1.0]])],"derivedFrom":subQ0})])]}),makeQuery(id+"F9L2YdqkWQCteiL_1.opExtrude","SWEPT_FACE",FACE,{"disambiguationData":[OSD([subQ0]),TDD([makeQuery(id+"F2.imprint","IMPRINT",EDGE,{"disambiguationData":[TD([[makeQuery(id+"F2.imprint","INTERSECT",VERTEX,{"derivedFrom":[subQ0,sQuery(id+"F2.wireOp",EDGE,"E18.0.71.0")]}),-1.0]])],"derivedFrom":subQ0})])]}),makeQuery(id+"F9L2YdqkWQCteiL_1.opExtrude","SWEPT_FACE",FACE,{"disambiguationData":[OSD([subQ0]),TDD([makeQuery(id+"F2.imprint","IMPRINT",EDGE,{"disambiguationData":[TD([[makeQuery(id+"F2.imprint","INTERSECT",VERTEX,{"derivedFrom":[subQ0,sQuery(id+"F2.wireOp",EDGE,"E18.0.73.0")]}),-1.0]])],"derivedFrom":subQ0})])]}),makeQuery(id+"F9L2YdqkWQCteiL_1.opExtrude","SWEPT_FACE",FACE,{"disambiguationData":[OSD([subQ0]),TDD([makeQuery(id+"F2.imprint","IMPRINT",EDGE,{"disambiguationData":[TD([[makeQuery(id+"F2.imprint","INTERSECT",VERTEX,{"derivedFrom":[subQ0,sQuery(id+"F2.wireOp",EDGE,"E18.0.75.0")]}),-1.0]])],"derivedFrom":subQ0})])]}),makeQuery(id+"F9L2YdqkWQCteiL_1.opExtrude","SWEPT_FACE",FACE,{"disambiguationData":[OSD([subQ0]),TDD([makeQuery(id+"F2.imprint","IMPRINT",EDGE,{"disambiguationData":[TD([[makeQuery(id+"F2.imprint","INTERSECT",VERTEX,{"derivedFrom":[subQ0,sQuery(id+"F2.wireOp",EDGE,"E18.0.77.0")]}),-1.0]])],"derivedFrom":subQ0})])]}),makeQuery(id+"F9L2YdqkWQCteiL_1.opExtrude","SWEPT_FACE",FACE,{"disambiguationData":[OSD([subQ0]),TDD([makeQuery(id+"F2.imprint","IMPRINT",EDGE,{"disambiguationData":[TD([[makeQuery(id+"F2.imprint","INTERSECT",VERTEX,{"derivedFrom":[subQ0,sQuery(id+"F2.wireOp",EDGE,"E18.0.79.0")]}),-1.0]])],"derivedFrom":subQ0})])]}),makeQuery(id+"F9L2YdqkWQCteiL_1.opExtrude","SWEPT_FACE",FACE,{"disambiguationData":[OSD([subQ0]),TDD([makeQuery(id+"F2.imprint","IMPRINT",EDGE,{"disambiguationData":[TD([[makeQuery(id+"F2.imprint","INTERSECT",VERTEX,{"derivedFrom":[subQ0,sQuery(id+"F2.wireOp",EDGE,"E18.0.81.0")]}),-1.0]])],"derivedFrom":subQ0})])]}),makeQuery(id+"F9L2YdqkWQCteiL_1.opExtrude","SWEPT_FACE",FACE,{"disambiguationData":[OSD([subQ0]),TDD([makeQuery(id+"F2.imprint","IMPRINT",EDGE,{"disambiguationData":[TD([[makeQuery(id+"F2.imprint","INTERSECT",VERTEX,{"derivedFrom":[subQ0,sQuery(id+"F2.wireOp",EDGE,"E18.0.83.0")]}),-1.0]])],"derivedFrom":subQ0})])]}),makeQuery(id+"F9L2YdqkWQCteiL_1.opExtrude","SWEPT_FACE",FACE,{"disambiguationData":[OSD([subQ0]),TDD([makeQuery(id+"F2.imprint","IMPRINT",EDGE,{"disambiguationData":[TD([[makeQuery(id+"F2.imprint","INTERSECT",VERTEX,{"derivedFrom":[subQ0,sQuery(id+"F2.wireOp",EDGE,"E18.0.85.0")]}),-1.0]])],"derivedFrom":subQ0})])]}),makeQuery(id+"F9L2YdqkWQCteiL_1.opExtrude","SWEPT_FACE",FACE,{"disambiguationData":[OSD([subQ0]),TDD([makeQuery(id+"F2.imprint","IMPRINT",EDGE,{"disambiguationData":[TD([[makeQuery(id+"F2.imprint","INTERSECT",VERTEX,{"derivedFrom":[subQ0,sQuery(id+"F2.wireOp",EDGE,"E18.0.87.0")]}),-1.0]])],"derivedFrom":subQ0})])]}),makeQuery(id+"F9L2YdqkWQCteiL_1.opExtrude","SWEPT_FACE",FACE,{"disambiguationData":[OSD([subQ0]),TDD([makeQuery(id+"F2.imprint","IMPRINT",EDGE,{"disambiguationData":[TD([[makeQuery(id+"F2.imprint","INTERSECT",VERTEX,{"derivedFrom":[subQ0,sQuery(id+"F2.wireOp",EDGE,"E18.0.89.0")]}),-1.0]])],"derivedFrom":subQ0})])]}),makeQuery(id+"F9L2YdqkWQCteiL_1.opExtrude","SWEPT_FACE",FACE,{"disambiguationData":[OSD([subQ0]),TDD([makeQuery(id+"F2.imprint","IMPRINT",EDGE,{"disambiguationData":[TD([[subQ1,1.0]])],"derivedFrom":subQ0}),makeQuery(id+"F2.imprint","IMPRINT",EDGE,{"disambiguationData":[TD([[subQ1,-1.0]])],"derivedFrom":subQ0})])]})]}),makeQuery(id+"F4.opExtrude","SWEPT_FACE",FACE,{"disambiguationData":[OSD([sQuery(id+"F3.wireOp",EDGE,"E23")])]})]}),makeQuery(id+"F6.opExtrude","SWEPT_FACE",FACE,{"disambiguationData":[OSD([sQuery(id+"F5.wireOp",EDGE,"E32"),sQuery(id+"F5.wireOp",EDGE,"E33")])]})]});}
            var sketch = newSketch(context, id + "F8", { "sketchPlane" : qUnion([Q0])});
            skLineSegment(sketch, "E35", {"start": v(0, 19.05) * mm, "end": v(7.62, 19.05) * mm});
            skLineSegment(sketch, "E36", {"start": v(7.62, 19.05) * mm, "end": v(7.62, 23.01) * mm});
            skLineSegment(sketch, "E37", {"start": v(7.62, 19.05) * mm, "end": v(7.62, 21.4) * mm});
            skPoint(sketch, "E38.orphan", {"position": v(15.24, 31.45) * mm});
            skPoint(sketch, "E39.visualSharp", {"position": v(7.62, 23.01) * mm});
            skPoint(sketch, "E40.visualSharp", {"position": v(15.24, 23.01) * mm});
            skLineSegment(sketch, "E41", {"start": v(7.62, 29.21) * mm, "end": v(15.24, 29.21) * mm});
            skPoint(sketch, "E42.endSnap0", {"position": v(7.62, 24.13) * mm});
            skLineSegment(sketch, "E43", {"start": v(11.43, 29.21) * mm, "end": v(11.43, 22.94) * mm});
            skLineSegment(sketch, "E44.MirrorCS", {"start": v(15.24, 19.05) * mm, "end": v(15.24, 23.01) * mm});
            skArc(sketch, "E45", {"start": v(10.24, 29.21) * mm, "mid": v(8.3, 26.38) * mm, "end": v(7.62, 23.01) * mm});
            skArc(sketch, "E46.MirrorCS", {"start": v(12.62, 29.21) * mm, "mid": v(14.56, 26.38) * mm, "end": v(15.24, 23.01) * mm});
            skLineSegment(sketch, "E47.MirrorCS", {"start": v(15.24, 19.05) * mm, "end": v(15.24, 21.4) * mm});
            skLineSegment(sketch, "E48", {"start": v(15.24, 19.05) * mm, "end": v(7.62, 19.05) * mm});
            skLineSegment(sketch, "E49", {"start": v(12.62, 29.21) * mm, "end": v(10.24, 29.21) * mm});
            skLineSegment(sketch, "E50.1.0.0", {"start": v(27.86, 29.21) * mm, "end": v(25.48, 29.21) * mm});
            skArc(sketch, "E50.1.0.1", {"start": v(25.48, 29.21) * mm, "mid": v(23.54, 26.38) * mm, "end": v(22.86, 23.01) * mm});
            skArc(sketch, "E50.1.0.2", {"start": v(27.86, 29.21) * mm, "mid": v(29.8, 26.38) * mm, "end": v(30.48, 23.01) * mm});
            skLineSegment(sketch, "E50.1.0.3", {"start": v(30.48, 19.05) * mm, "end": v(30.48, 23.01) * mm});
            skLineSegment(sketch, "E50.1.0.4", {"start": v(22.86, 19.05) * mm, "end": v(22.86, 23.01) * mm});
            skLineSegment(sketch, "E50.1.0.5", {"start": v(30.48, 19.05) * mm, "end": v(22.86, 19.05) * mm});
            skLineSegment(sketch, "E50.2.0.0", {"start": v(43.1, 29.21) * mm, "end": v(40.72, 29.21) * mm});
            skArc(sketch, "E50.2.0.1", {"start": v(40.72, 29.21) * mm, "mid": v(38.78, 26.38) * mm, "end": v(38.1, 23.01) * mm});
            skArc(sketch, "E50.2.0.2", {"start": v(43.1, 29.21) * mm, "mid": v(45.04, 26.38) * mm, "end": v(45.72, 23.01) * mm});
            skLineSegment(sketch, "E50.2.0.3", {"start": v(45.72, 19.05) * mm, "end": v(45.72, 23.01) * mm});
            skLineSegment(sketch, "E50.2.0.4", {"start": v(38.1, 19.05) * mm, "end": v(38.1, 23.01) * mm});
            skLineSegment(sketch, "E50.2.0.5", {"start": v(45.72, 19.05) * mm, "end": v(38.1, 19.05) * mm});
            skLineSegment(sketch, "E50.3.0.0", {"start": v(58.34, 29.21) * mm, "end": v(55.96, 29.21) * mm});
            skArc(sketch, "E50.3.0.1", {"start": v(55.96, 29.21) * mm, "mid": v(54.02, 26.38) * mm, "end": v(53.34, 23.01) * mm});
            skArc(sketch, "E50.3.0.2", {"start": v(58.34, 29.21) * mm, "mid": v(60.28, 26.38) * mm, "end": v(60.96, 23.01) * mm});
            skLineSegment(sketch, "E50.3.0.3", {"start": v(60.96, 19.05) * mm, "end": v(60.96, 23.01) * mm});
            skLineSegment(sketch, "E50.3.0.4", {"start": v(53.34, 19.05) * mm, "end": v(53.34, 23.01) * mm});
            skLineSegment(sketch, "E50.3.0.5", {"start": v(60.96, 19.05) * mm, "end": v(53.34, 19.05) * mm});
            skLineSegment(sketch, "E50.4.0.0", {"start": v(73.58, 29.21) * mm, "end": v(71.2, 29.21) * mm});
            skArc(sketch, "E50.4.0.1", {"start": v(71.2, 29.21) * mm, "mid": v(69.26, 26.38) * mm, "end": v(68.58, 23.01) * mm});
            skArc(sketch, "E50.4.0.2", {"start": v(73.58, 29.21) * mm, "mid": v(75.52, 26.38) * mm, "end": v(76.2, 23.01) * mm});
            skLineSegment(sketch, "E50.4.0.3", {"start": v(76.2, 19.05) * mm, "end": v(76.2, 23.01) * mm});
            skLineSegment(sketch, "E50.4.0.4", {"start": v(68.58, 19.05) * mm, "end": v(68.58, 23.01) * mm});
            skLineSegment(sketch, "E50.4.0.5", {"start": v(76.2, 19.05) * mm, "end": v(68.58, 19.05) * mm});
            skLineSegment(sketch, "E50.5.0.0", {"start": v(88.82, 29.21) * mm, "end": v(86.44, 29.21) * mm});
            skArc(sketch, "E50.5.0.1", {"start": v(86.44, 29.21) * mm, "mid": v(84.5, 26.38) * mm, "end": v(83.82, 23.01) * mm});
            skArc(sketch, "E50.5.0.2", {"start": v(88.82, 29.21) * mm, "mid": v(90.76, 26.38) * mm, "end": v(91.44, 23.01) * mm});
            skLineSegment(sketch, "E50.5.0.3", {"start": v(91.44, 19.05) * mm, "end": v(91.44, 23.01) * mm});
            skLineSegment(sketch, "E50.5.0.4", {"start": v(83.82, 19.05) * mm, "end": v(83.82, 23.01) * mm});
            skLineSegment(sketch, "E50.5.0.5", {"start": v(91.44, 19.05) * mm, "end": v(83.82, 19.05) * mm});
            skLineSegment(sketch, "E50.6.0.0", {"start": v(104.06, 29.21) * mm, "end": v(101.68, 29.21) * mm});
            skArc(sketch, "E50.6.0.1", {"start": v(101.68, 29.21) * mm, "mid": v(99.74, 26.38) * mm, "end": v(99.06, 23.01) * mm});
            skArc(sketch, "E50.6.0.2", {"start": v(104.06, 29.21) * mm, "mid": v(106, 26.38) * mm, "end": v(106.68, 23.01) * mm});
            skLineSegment(sketch, "E50.6.0.3", {"start": v(106.68, 19.05) * mm, "end": v(106.68, 23.01) * mm});
            skLineSegment(sketch, "E50.6.0.4", {"start": v(99.06, 19.05) * mm, "end": v(99.06, 23.01) * mm});
            skLineSegment(sketch, "E50.6.0.5", {"start": v(106.68, 19.05) * mm, "end": v(99.06, 19.05) * mm});
            skLineSegment(sketch, "E50.7.0.0", {"start": v(119.3, 29.21) * mm, "end": v(116.92, 29.21) * mm});
            skArc(sketch, "E50.7.0.1", {"start": v(116.92, 29.21) * mm, "mid": v(114.98, 26.38) * mm, "end": v(114.3, 23.01) * mm});
            skArc(sketch, "E50.7.0.2", {"start": v(119.3, 29.21) * mm, "mid": v(121.24, 26.38) * mm, "end": v(121.92, 23.01) * mm});
            skLineSegment(sketch, "E50.7.0.3", {"start": v(121.92, 19.05) * mm, "end": v(121.92, 23.01) * mm});
            skLineSegment(sketch, "E50.7.0.4", {"start": v(114.3, 19.05) * mm, "end": v(114.3, 23.01) * mm});
            skLineSegment(sketch, "E50.7.0.5", {"start": v(121.92, 19.05) * mm, "end": v(114.3, 19.05) * mm});
            skLineSegment(sketch, "E50.8.0.0", {"start": v(134.54, 29.21) * mm, "end": v(132.16, 29.21) * mm});
            skArc(sketch, "E50.8.0.1", {"start": v(132.16, 29.21) * mm, "mid": v(130.22, 26.38) * mm, "end": v(129.54, 23.01) * mm});
            skArc(sketch, "E50.8.0.2", {"start": v(134.54, 29.21) * mm, "mid": v(136.48, 26.38) * mm, "end": v(137.16, 23.01) * mm});
            skLineSegment(sketch, "E50.8.0.3", {"start": v(137.16, 19.05) * mm, "end": v(137.16, 23.01) * mm});
            skLineSegment(sketch, "E50.8.0.4", {"start": v(129.54, 19.05) * mm, "end": v(129.54, 23.01) * mm});
            skLineSegment(sketch, "E50.8.0.5", {"start": v(137.16, 19.05) * mm, "end": v(129.54, 19.05) * mm});
            skLineSegment(sketch, "E50.9.0.0", {"start": v(149.78, 29.21) * mm, "end": v(147.4, 29.21) * mm});
            skArc(sketch, "E50.9.0.1", {"start": v(147.4, 29.21) * mm, "mid": v(145.46, 26.38) * mm, "end": v(144.78, 23.01) * mm});
            skArc(sketch, "E50.9.0.2", {"start": v(149.78, 29.21) * mm, "mid": v(151.72, 26.38) * mm, "end": v(152.4, 23.01) * mm});
            skLineSegment(sketch, "E50.9.0.3", {"start": v(152.4, 19.05) * mm, "end": v(152.4, 23.01) * mm});
            skLineSegment(sketch, "E50.9.0.4", {"start": v(144.78, 19.05) * mm, "end": v(144.78, 23.01) * mm});
            skLineSegment(sketch, "E50.9.0.5", {"start": v(152.4, 19.05) * mm, "end": v(144.78, 19.05) * mm});
            skLineSegment(sketch, "E50.10.0.0", {"start": v(165.02, 29.21) * mm, "end": v(162.64, 29.21) * mm});
            skArc(sketch, "E50.10.0.1", {"start": v(162.64, 29.21) * mm, "mid": v(160.7, 26.38) * mm, "end": v(160.02, 23.01) * mm});
            skArc(sketch, "E50.10.0.2", {"start": v(165.02, 29.21) * mm, "mid": v(166.96, 26.38) * mm, "end": v(167.64, 23.01) * mm});
            skLineSegment(sketch, "E50.10.0.3", {"start": v(167.64, 19.05) * mm, "end": v(167.64, 23.01) * mm});
            skLineSegment(sketch, "E50.10.0.4", {"start": v(160.02, 19.05) * mm, "end": v(160.02, 23.01) * mm});
            skLineSegment(sketch, "E50.10.0.5", {"start": v(167.64, 19.05) * mm, "end": v(160.02, 19.05) * mm});
            skLineSegment(sketch, "E50.11.0.0", {"start": v(180.26, 29.21) * mm, "end": v(177.88, 29.21) * mm});
            skArc(sketch, "E50.11.0.1", {"start": v(177.88, 29.21) * mm, "mid": v(175.94, 26.38) * mm, "end": v(175.26, 23.01) * mm});
            skArc(sketch, "E50.11.0.2", {"start": v(180.26, 29.21) * mm, "mid": v(182.2, 26.38) * mm, "end": v(182.88, 23.01) * mm});
            skLineSegment(sketch, "E50.11.0.3", {"start": v(182.88, 19.05) * mm, "end": v(182.88, 23.01) * mm});
            skLineSegment(sketch, "E50.11.0.4", {"start": v(175.26, 19.05) * mm, "end": v(175.26, 23.01) * mm});
            skLineSegment(sketch, "E50.11.0.5", {"start": v(182.88, 19.05) * mm, "end": v(175.26, 19.05) * mm});
            skLineSegment(sketch, "E50.12.0.0", {"start": v(195.5, 29.21) * mm, "end": v(193.12, 29.21) * mm});
            skArc(sketch, "E50.12.0.1", {"start": v(193.12, 29.21) * mm, "mid": v(191.18, 26.38) * mm, "end": v(190.5, 23.01) * mm});
            skArc(sketch, "E50.12.0.2", {"start": v(195.5, 29.21) * mm, "mid": v(197.44, 26.38) * mm, "end": v(198.12, 23.01) * mm});
            skLineSegment(sketch, "E50.12.0.3", {"start": v(198.12, 19.05) * mm, "end": v(198.12, 23.01) * mm});
            skLineSegment(sketch, "E50.12.0.4", {"start": v(190.5, 19.05) * mm, "end": v(190.5, 23.01) * mm});
            skLineSegment(sketch, "E50.12.0.5", {"start": v(198.12, 19.05) * mm, "end": v(190.5, 19.05) * mm});
            skLineSegment(sketch, "E50.13.0.0", {"start": v(210.74, 29.21) * mm, "end": v(208.36, 29.21) * mm});
            skArc(sketch, "E50.13.0.1", {"start": v(208.36, 29.21) * mm, "mid": v(206.42, 26.38) * mm, "end": v(205.74, 23.01) * mm});
            skArc(sketch, "E50.13.0.2", {"start": v(210.74, 29.21) * mm, "mid": v(212.68, 26.38) * mm, "end": v(213.36, 23.01) * mm});
            skLineSegment(sketch, "E50.13.0.3", {"start": v(213.36, 19.05) * mm, "end": v(213.36, 23.01) * mm});
            skLineSegment(sketch, "E50.13.0.4", {"start": v(205.74, 19.05) * mm, "end": v(205.74, 23.01) * mm});
            skLineSegment(sketch, "E50.13.0.5", {"start": v(213.36, 19.05) * mm, "end": v(205.74, 19.05) * mm});
            skLineSegment(sketch, "E50.14.0.0", {"start": v(225.98, 29.21) * mm, "end": v(223.6, 29.21) * mm});
            skArc(sketch, "E50.14.0.1", {"start": v(223.6, 29.21) * mm, "mid": v(221.66, 26.38) * mm, "end": v(220.98, 23.01) * mm});
            skArc(sketch, "E50.14.0.2", {"start": v(225.98, 29.21) * mm, "mid": v(227.92, 26.38) * mm, "end": v(228.6, 23.01) * mm});
            skLineSegment(sketch, "E50.14.0.3", {"start": v(228.6, 19.05) * mm, "end": v(228.6, 23.01) * mm});
            skLineSegment(sketch, "E50.14.0.4", {"start": v(220.98, 19.05) * mm, "end": v(220.98, 23.01) * mm});
            skLineSegment(sketch, "E50.14.0.5", {"start": v(228.6, 19.05) * mm, "end": v(220.98, 19.05) * mm});
            skLineSegment(sketch, "E50.15.0.0", {"start": v(241.22, 29.21) * mm, "end": v(238.84, 29.21) * mm});
            skArc(sketch, "E50.15.0.1", {"start": v(238.84, 29.21) * mm, "mid": v(236.9, 26.38) * mm, "end": v(236.22, 23.01) * mm});
            skArc(sketch, "E50.15.0.2", {"start": v(241.22, 29.21) * mm, "mid": v(243.16, 26.38) * mm, "end": v(243.84, 23.01) * mm});
            skLineSegment(sketch, "E50.15.0.3", {"start": v(243.84, 19.05) * mm, "end": v(243.84, 23.01) * mm});
            skLineSegment(sketch, "E50.15.0.4", {"start": v(236.22, 19.05) * mm, "end": v(236.22, 23.01) * mm});
            skLineSegment(sketch, "E50.15.0.5", {"start": v(243.84, 19.05) * mm, "end": v(236.22, 19.05) * mm});
            skLineSegment(sketch, "E50.16.0.0", {"start": v(256.46, 29.21) * mm, "end": v(254.08, 29.21) * mm});
            skArc(sketch, "E50.16.0.1", {"start": v(254.08, 29.21) * mm, "mid": v(252.14, 26.38) * mm, "end": v(251.46, 23.01) * mm});
            skArc(sketch, "E50.16.0.2", {"start": v(256.46, 29.21) * mm, "mid": v(258.4, 26.38) * mm, "end": v(259.08, 23.01) * mm});
            skLineSegment(sketch, "E50.16.0.3", {"start": v(259.08, 19.05) * mm, "end": v(259.08, 23.01) * mm});
            skLineSegment(sketch, "E50.16.0.4", {"start": v(251.46, 19.05) * mm, "end": v(251.46, 23.01) * mm});
            skLineSegment(sketch, "E50.16.0.5", {"start": v(259.08, 19.05) * mm, "end": v(251.46, 19.05) * mm});
            skLineSegment(sketch, "E50.17.0.0", {"start": v(271.7, 29.21) * mm, "end": v(269.32, 29.21) * mm});
            skArc(sketch, "E50.17.0.1", {"start": v(269.32, 29.21) * mm, "mid": v(267.38, 26.38) * mm, "end": v(266.7, 23.01) * mm});
            skArc(sketch, "E50.17.0.2", {"start": v(271.7, 29.21) * mm, "mid": v(273.64, 26.38) * mm, "end": v(274.32, 23.01) * mm});
            skLineSegment(sketch, "E50.17.0.3", {"start": v(274.32, 19.05) * mm, "end": v(274.32, 23.01) * mm});
            skLineSegment(sketch, "E50.17.0.4", {"start": v(266.7, 19.05) * mm, "end": v(266.7, 23.01) * mm});
            skLineSegment(sketch, "E50.17.0.5", {"start": v(274.32, 19.05) * mm, "end": v(266.7, 19.05) * mm});
            skLineSegment(sketch, "E50.18.0.0", {"start": v(286.94, 29.21) * mm, "end": v(284.56, 29.21) * mm});
            skArc(sketch, "E50.18.0.1", {"start": v(284.56, 29.21) * mm, "mid": v(282.62, 26.38) * mm, "end": v(281.94, 23.01) * mm});
            skArc(sketch, "E50.18.0.2", {"start": v(286.94, 29.21) * mm, "mid": v(288.88, 26.38) * mm, "end": v(289.56, 23.01) * mm});
            skLineSegment(sketch, "E50.18.0.3", {"start": v(289.56, 19.05) * mm, "end": v(289.56, 23.01) * mm});
            skLineSegment(sketch, "E50.18.0.4", {"start": v(281.94, 19.05) * mm, "end": v(281.94, 23.01) * mm});
            skLineSegment(sketch, "E50.18.0.5", {"start": v(289.56, 19.05) * mm, "end": v(281.94, 19.05) * mm});
            skLineSegment(sketch, "E50.19.0.0", {"start": v(302.18, 29.21) * mm, "end": v(299.8, 29.21) * mm});
            skArc(sketch, "E50.19.0.1", {"start": v(299.8, 29.21) * mm, "mid": v(297.86, 26.38) * mm, "end": v(297.18, 23.01) * mm});
            skArc(sketch, "E50.19.0.2", {"start": v(302.18, 29.21) * mm, "mid": v(304.12, 26.38) * mm, "end": v(304.8, 23.01) * mm});
            skLineSegment(sketch, "E50.19.0.3", {"start": v(304.8, 19.05) * mm, "end": v(304.8, 23.01) * mm});
            skLineSegment(sketch, "E50.19.0.4", {"start": v(297.18, 19.05) * mm, "end": v(297.18, 23.01) * mm});
            skLineSegment(sketch, "E50.19.0.5", {"start": v(304.8, 19.05) * mm, "end": v(297.18, 19.05) * mm});
            skLineSegment(sketch, "E50.20.0.0", {"start": v(317.42, 29.21) * mm, "end": v(315.04, 29.21) * mm});
            skArc(sketch, "E50.20.0.1", {"start": v(315.04, 29.21) * mm, "mid": v(313.1, 26.38) * mm, "end": v(312.42, 23.01) * mm});
            skArc(sketch, "E50.20.0.2", {"start": v(317.42, 29.21) * mm, "mid": v(319.36, 26.38) * mm, "end": v(320.04, 23.01) * mm});
            skLineSegment(sketch, "E50.20.0.3", {"start": v(320.04, 19.05) * mm, "end": v(320.04, 23.01) * mm});
            skLineSegment(sketch, "E50.20.0.4", {"start": v(312.42, 19.05) * mm, "end": v(312.42, 23.01) * mm});
            skLineSegment(sketch, "E50.20.0.5", {"start": v(320.04, 19.05) * mm, "end": v(312.42, 19.05) * mm});
            skLineSegment(sketch, "E50.21.0.0", {"start": v(332.66, 29.21) * mm, "end": v(330.28, 29.21) * mm});
            skArc(sketch, "E50.21.0.1", {"start": v(330.28, 29.21) * mm, "mid": v(328.34, 26.38) * mm, "end": v(327.66, 23.01) * mm});
            skArc(sketch, "E50.21.0.2", {"start": v(332.66, 29.21) * mm, "mid": v(334.6, 26.38) * mm, "end": v(335.28, 23.01) * mm});
            skLineSegment(sketch, "E50.21.0.3", {"start": v(335.28, 19.05) * mm, "end": v(335.28, 23.01) * mm});
            skLineSegment(sketch, "E50.21.0.4", {"start": v(327.66, 19.05) * mm, "end": v(327.66, 23.01) * mm});
            skLineSegment(sketch, "E50.21.0.5", {"start": v(335.28, 19.05) * mm, "end": v(327.66, 19.05) * mm});
            skLineSegment(sketch, "E50.22.0.0", {"start": v(347.9, 29.21) * mm, "end": v(345.52, 29.21) * mm});
            skArc(sketch, "E50.22.0.1", {"start": v(345.52, 29.21) * mm, "mid": v(343.58, 26.38) * mm, "end": v(342.9, 23.01) * mm});
            skArc(sketch, "E50.22.0.2", {"start": v(347.9, 29.21) * mm, "mid": v(349.84, 26.38) * mm, "end": v(350.52, 23.01) * mm});
            skLineSegment(sketch, "E50.22.0.3", {"start": v(350.52, 19.05) * mm, "end": v(350.52, 23.01) * mm});
            skLineSegment(sketch, "E50.22.0.4", {"start": v(342.9, 19.05) * mm, "end": v(342.9, 23.01) * mm});
            skLineSegment(sketch, "E50.22.0.5", {"start": v(350.52, 19.05) * mm, "end": v(342.9, 19.05) * mm});
            skLineSegment(sketch, "E50.23.0.0", {"start": v(363.14, 29.21) * mm, "end": v(360.76, 29.21) * mm});
            skArc(sketch, "E50.23.0.1", {"start": v(360.76, 29.21) * mm, "mid": v(358.82, 26.38) * mm, "end": v(358.14, 23.01) * mm});
            skArc(sketch, "E50.23.0.2", {"start": v(363.14, 29.21) * mm, "mid": v(365.08, 26.38) * mm, "end": v(365.76, 23.01) * mm});
            skLineSegment(sketch, "E50.23.0.3", {"start": v(365.76, 19.05) * mm, "end": v(365.76, 23.01) * mm});
            skLineSegment(sketch, "E50.23.0.4", {"start": v(358.14, 19.05) * mm, "end": v(358.14, 23.01) * mm});
            skLineSegment(sketch, "E50.23.0.5", {"start": v(365.76, 19.05) * mm, "end": v(358.14, 19.05) * mm});
            skLineSegment(sketch, "E50.24.0.0", {"start": v(378.38, 29.21) * mm, "end": v(376, 29.21) * mm});
            skArc(sketch, "E50.24.0.1", {"start": v(376, 29.21) * mm, "mid": v(374.06, 26.38) * mm, "end": v(373.38, 23.01) * mm});
            skArc(sketch, "E50.24.0.2", {"start": v(378.38, 29.21) * mm, "mid": v(380.32, 26.38) * mm, "end": v(381, 23.01) * mm});
            skLineSegment(sketch, "E50.24.0.3", {"start": v(381, 19.05) * mm, "end": v(381, 23.01) * mm});
            skLineSegment(sketch, "E50.24.0.4", {"start": v(373.38, 19.05) * mm, "end": v(373.38, 23.01) * mm});
            skLineSegment(sketch, "E50.24.0.5", {"start": v(381, 19.05) * mm, "end": v(373.38, 19.05) * mm});
            skLineSegment(sketch, "E50.25.0.0", {"start": v(393.62, 29.21) * mm, "end": v(391.24, 29.21) * mm});
            skArc(sketch, "E50.25.0.1", {"start": v(391.24, 29.21) * mm, "mid": v(389.3, 26.38) * mm, "end": v(388.62, 23.01) * mm});
            skArc(sketch, "E50.25.0.2", {"start": v(393.62, 29.21) * mm, "mid": v(395.56, 26.38) * mm, "end": v(396.24, 23.01) * mm});
            skLineSegment(sketch, "E50.25.0.3", {"start": v(396.24, 19.05) * mm, "end": v(396.24, 23.01) * mm});
            skLineSegment(sketch, "E50.25.0.4", {"start": v(388.62, 19.05) * mm, "end": v(388.62, 23.01) * mm});
            skLineSegment(sketch, "E50.25.0.5", {"start": v(396.24, 19.05) * mm, "end": v(388.62, 19.05) * mm});
            skLineSegment(sketch, "E50.26.0.0", {"start": v(408.86, 29.21) * mm, "end": v(406.48, 29.21) * mm});
            skArc(sketch, "E50.26.0.1", {"start": v(406.48, 29.21) * mm, "mid": v(404.54, 26.38) * mm, "end": v(403.86, 23.01) * mm});
            skArc(sketch, "E50.26.0.2", {"start": v(408.86, 29.21) * mm, "mid": v(410.8, 26.38) * mm, "end": v(411.48, 23.01) * mm});
            skLineSegment(sketch, "E50.26.0.3", {"start": v(411.48, 19.05) * mm, "end": v(411.48, 23.01) * mm});
            skLineSegment(sketch, "E50.26.0.4", {"start": v(403.86, 19.05) * mm, "end": v(403.86, 23.01) * mm});
            skLineSegment(sketch, "E50.26.0.5", {"start": v(411.48, 19.05) * mm, "end": v(403.86, 19.05) * mm});
            skLineSegment(sketch, "E50.27.0.0", {"start": v(424.1, 29.21) * mm, "end": v(421.72, 29.21) * mm});
            skArc(sketch, "E50.27.0.1", {"start": v(421.72, 29.21) * mm, "mid": v(419.78, 26.38) * mm, "end": v(419.1, 23.01) * mm});
            skArc(sketch, "E50.27.0.2", {"start": v(424.1, 29.21) * mm, "mid": v(426.04, 26.38) * mm, "end": v(426.72, 23.01) * mm});
            skLineSegment(sketch, "E50.27.0.3", {"start": v(426.72, 19.05) * mm, "end": v(426.72, 23.01) * mm});
            skLineSegment(sketch, "E50.27.0.4", {"start": v(419.1, 19.05) * mm, "end": v(419.1, 23.01) * mm});
            skLineSegment(sketch, "E50.27.0.5", {"start": v(426.72, 19.05) * mm, "end": v(419.1, 19.05) * mm});
            skLineSegment(sketch, "E50.28.0.0", {"start": v(439.34, 29.21) * mm, "end": v(436.96, 29.21) * mm});
            skArc(sketch, "E50.28.0.1", {"start": v(436.96, 29.21) * mm, "mid": v(435.02, 26.38) * mm, "end": v(434.34, 23.01) * mm});
            skArc(sketch, "E50.28.0.2", {"start": v(439.34, 29.21) * mm, "mid": v(441.28, 26.38) * mm, "end": v(441.96, 23.01) * mm});
            skLineSegment(sketch, "E50.28.0.3", {"start": v(441.96, 19.05) * mm, "end": v(441.96, 23.01) * mm});
            skLineSegment(sketch, "E50.28.0.4", {"start": v(434.34, 19.05) * mm, "end": v(434.34, 23.01) * mm});
            skLineSegment(sketch, "E50.28.0.5", {"start": v(441.96, 19.05) * mm, "end": v(434.34, 19.05) * mm});
            skLineSegment(sketch, "E50.29.0.0", {"start": v(454.58, 29.21) * mm, "end": v(452.2, 29.21) * mm});
            skArc(sketch, "E50.29.0.1", {"start": v(452.2, 29.21) * mm, "mid": v(450.26, 26.38) * mm, "end": v(449.58, 23.01) * mm});
            skArc(sketch, "E50.29.0.2", {"start": v(454.58, 29.21) * mm, "mid": v(456.52, 26.38) * mm, "end": v(457.2, 23.01) * mm});
            skLineSegment(sketch, "E50.29.0.3", {"start": v(457.2, 19.05) * mm, "end": v(457.2, 23.01) * mm});
            skLineSegment(sketch, "E50.29.0.4", {"start": v(449.58, 19.05) * mm, "end": v(449.58, 23.01) * mm});
            skLineSegment(sketch, "E50.29.0.5", {"start": v(457.2, 19.05) * mm, "end": v(449.58, 19.05) * mm});
            skLineSegment(sketch, "E50.30.0.0", {"start": v(469.82, 29.21) * mm, "end": v(467.44, 29.21) * mm});
            skArc(sketch, "E50.30.0.1", {"start": v(467.44, 29.21) * mm, "mid": v(465.5, 26.38) * mm, "end": v(464.82, 23.01) * mm});
            skArc(sketch, "E50.30.0.2", {"start": v(469.82, 29.21) * mm, "mid": v(471.76, 26.38) * mm, "end": v(472.44, 23.01) * mm});
            skLineSegment(sketch, "E50.30.0.3", {"start": v(472.44, 19.05) * mm, "end": v(472.44, 23.01) * mm});
            skLineSegment(sketch, "E50.30.0.4", {"start": v(464.82, 19.05) * mm, "end": v(464.82, 23.01) * mm});
            skLineSegment(sketch, "E50.30.0.5", {"start": v(472.44, 19.05) * mm, "end": v(464.82, 19.05) * mm});
            skLineSegment(sketch, "E50.31.0.0", {"start": v(485.06, 29.21) * mm, "end": v(482.68, 29.21) * mm});
            skArc(sketch, "E50.31.0.1", {"start": v(482.68, 29.21) * mm, "mid": v(480.74, 26.38) * mm, "end": v(480.06, 23.01) * mm});
            skArc(sketch, "E50.31.0.2", {"start": v(485.06, 29.21) * mm, "mid": v(487, 26.38) * mm, "end": v(487.68, 23.01) * mm});
            skLineSegment(sketch, "E50.31.0.3", {"start": v(487.68, 19.05) * mm, "end": v(487.68, 23.01) * mm});
            skLineSegment(sketch, "E50.31.0.4", {"start": v(480.06, 19.05) * mm, "end": v(480.06, 23.01) * mm});
            skLineSegment(sketch, "E50.31.0.5", {"start": v(487.68, 19.05) * mm, "end": v(480.06, 19.05) * mm});
            skLineSegment(sketch, "E50.32.0.0", {"start": v(500.3, 29.21) * mm, "end": v(497.92, 29.21) * mm});
            skArc(sketch, "E50.32.0.1", {"start": v(497.92, 29.21) * mm, "mid": v(495.98, 26.38) * mm, "end": v(495.3, 23.01) * mm});
            skArc(sketch, "E50.32.0.2", {"start": v(500.3, 29.2) * mm, "mid": v(502.24, 26.38) * mm, "end": v(502.92, 23.01) * mm});
            skLineSegment(sketch, "E50.32.0.3", {"start": v(502.92, 19.05) * mm, "end": v(502.92, 23.01) * mm});
            skLineSegment(sketch, "E50.32.0.4", {"start": v(495.3, 19.05) * mm, "end": v(495.3, 23.01) * mm});
            skLineSegment(sketch, "E50.32.0.5", {"start": v(502.92, 19.05) * mm, "end": v(495.3, 19.05) * mm});
            skLineSegment(sketch, "E50.33.0.0", {"start": v(515.54, 29.21) * mm, "end": v(513.16, 29.21) * mm});
            skArc(sketch, "E50.33.0.1", {"start": v(513.16, 29.21) * mm, "mid": v(511.22, 26.38) * mm, "end": v(510.54, 23.01) * mm});
            skArc(sketch, "E50.33.0.2", {"start": v(515.54, 29.21) * mm, "mid": v(517.48, 26.38) * mm, "end": v(518.16, 23.01) * mm});
            skLineSegment(sketch, "E50.33.0.3", {"start": v(518.16, 19.05) * mm, "end": v(518.16, 23.01) * mm});
            skLineSegment(sketch, "E50.33.0.4", {"start": v(510.54, 19.05) * mm, "end": v(510.54, 23.01) * mm});
            skLineSegment(sketch, "E50.33.0.5", {"start": v(518.16, 19.05) * mm, "end": v(510.54, 19.05) * mm});
            skLineSegment(sketch, "E50.34.0.0", {"start": v(530.78, 29.21) * mm, "end": v(528.4, 29.21) * mm});
            skArc(sketch, "E50.34.0.1", {"start": v(528.4, 29.21) * mm, "mid": v(526.46, 26.38) * mm, "end": v(525.78, 23.01) * mm});
            skArc(sketch, "E50.34.0.2", {"start": v(530.78, 29.21) * mm, "mid": v(532.72, 26.38) * mm, "end": v(533.4, 23.01) * mm});
            skLineSegment(sketch, "E50.34.0.3", {"start": v(533.4, 19.05) * mm, "end": v(533.4, 23.01) * mm});
            skLineSegment(sketch, "E50.34.0.4", {"start": v(525.78, 19.05) * mm, "end": v(525.78, 23.01) * mm});
            skLineSegment(sketch, "E50.34.0.5", {"start": v(533.4, 19.05) * mm, "end": v(525.78, 19.05) * mm});
            skLineSegment(sketch, "E50.35.0.0", {"start": v(546.02, 29.21) * mm, "end": v(543.64, 29.21) * mm});
            skArc(sketch, "E50.35.0.1", {"start": v(543.64, 29.21) * mm, "mid": v(541.7, 26.38) * mm, "end": v(541.02, 23.01) * mm});
            skArc(sketch, "E50.35.0.2", {"start": v(546.02, 29.21) * mm, "mid": v(547.96, 26.38) * mm, "end": v(548.64, 23.01) * mm});
            skLineSegment(sketch, "E50.35.0.3", {"start": v(548.64, 19.05) * mm, "end": v(548.64, 23.01) * mm});
            skLineSegment(sketch, "E50.35.0.4", {"start": v(541.02, 19.05) * mm, "end": v(541.02, 23.01) * mm});
            skLineSegment(sketch, "E50.35.0.5", {"start": v(548.64, 19.05) * mm, "end": v(541.02, 19.05) * mm});
            skLineSegment(sketch, "E50.36.0.0", {"start": v(561.26, 29.21) * mm, "end": v(558.88, 29.21) * mm});
            skArc(sketch, "E50.36.0.1", {"start": v(558.88, 29.21) * mm, "mid": v(556.94, 26.38) * mm, "end": v(556.26, 23.01) * mm});
            skArc(sketch, "E50.36.0.2", {"start": v(561.26, 29.21) * mm, "mid": v(563.2, 26.38) * mm, "end": v(563.88, 23.01) * mm});
            skLineSegment(sketch, "E50.36.0.3", {"start": v(563.88, 19.05) * mm, "end": v(563.88, 23.01) * mm});
            skLineSegment(sketch, "E50.36.0.4", {"start": v(556.26, 19.05) * mm, "end": v(556.26, 23.01) * mm});
            skLineSegment(sketch, "E50.36.0.5", {"start": v(563.88, 19.05) * mm, "end": v(556.26, 19.05) * mm});
            skLineSegment(sketch, "E50.37.0.0", {"start": v(576.5, 29.21) * mm, "end": v(574.12, 29.21) * mm});
            skArc(sketch, "E50.37.0.1", {"start": v(574.12, 29.21) * mm, "mid": v(572.18, 26.38) * mm, "end": v(571.5, 23.01) * mm});
            skArc(sketch, "E50.37.0.2", {"start": v(576.5, 29.21) * mm, "mid": v(578.44, 26.38) * mm, "end": v(579.12, 23.01) * mm});
            skLineSegment(sketch, "E50.37.0.3", {"start": v(579.12, 19.05) * mm, "end": v(579.12, 23.01) * mm});
            skLineSegment(sketch, "E50.37.0.4", {"start": v(571.5, 19.05) * mm, "end": v(571.5, 23.01) * mm});
            skLineSegment(sketch, "E50.37.0.5", {"start": v(579.12, 19.05) * mm, "end": v(571.5, 19.05) * mm});
            skLineSegment(sketch, "E50.38.0.0", {"start": v(591.74, 29.21) * mm, "end": v(589.36, 29.21) * mm});
            skArc(sketch, "E50.38.0.1", {"start": v(589.36, 29.21) * mm, "mid": v(587.42, 26.38) * mm, "end": v(586.74, 23.01) * mm});
            skArc(sketch, "E50.38.0.2", {"start": v(591.74, 29.21) * mm, "mid": v(593.68, 26.38) * mm, "end": v(594.36, 23.01) * mm});
            skLineSegment(sketch, "E50.38.0.3", {"start": v(594.36, 19.05) * mm, "end": v(594.36, 23.01) * mm});
            skLineSegment(sketch, "E50.38.0.4", {"start": v(586.74, 19.05) * mm, "end": v(586.74, 23.01) * mm});
            skLineSegment(sketch, "E50.38.0.5", {"start": v(594.36, 19.05) * mm, "end": v(586.74, 19.05) * mm});
            skLineSegment(sketch, "E50.39.0.0", {"start": v(606.98, 29.21) * mm, "end": v(604.6, 29.21) * mm});
            skArc(sketch, "E50.39.0.1", {"start": v(604.6, 29.21) * mm, "mid": v(602.66, 26.38) * mm, "end": v(601.98, 23.01) * mm});
            skArc(sketch, "E50.39.0.2", {"start": v(606.98, 29.21) * mm, "mid": v(608.92, 26.38) * mm, "end": v(609.6, 23.01) * mm});
            skLineSegment(sketch, "E50.39.0.3", {"start": v(609.6, 19.05) * mm, "end": v(609.6, 23.01) * mm});
            skLineSegment(sketch, "E50.39.0.4", {"start": v(601.98, 19.05) * mm, "end": v(601.98, 23.01) * mm});
            skLineSegment(sketch, "E50.39.0.5", {"start": v(609.6, 19.05) * mm, "end": v(601.98, 19.05) * mm});
            skLineSegment(sketch, "E50.40.0.0", {"start": v(622.22, 29.21) * mm, "end": v(619.84, 29.21) * mm});
            skArc(sketch, "E50.40.0.1", {"start": v(619.84, 29.21) * mm, "mid": v(617.9, 26.38) * mm, "end": v(617.22, 23.01) * mm});
            skArc(sketch, "E50.40.0.2", {"start": v(622.22, 29.21) * mm, "mid": v(624.16, 26.38) * mm, "end": v(624.84, 23.01) * mm});
            skLineSegment(sketch, "E50.40.0.3", {"start": v(624.84, 19.05) * mm, "end": v(624.84, 23.01) * mm});
            skLineSegment(sketch, "E50.40.0.4", {"start": v(617.22, 19.05) * mm, "end": v(617.22, 23.01) * mm});
            skLineSegment(sketch, "E50.40.0.5", {"start": v(624.84, 19.05) * mm, "end": v(617.22, 19.05) * mm});
            skLineSegment(sketch, "E50.41.0.0", {"start": v(637.46, 29.21) * mm, "end": v(635.08, 29.21) * mm});
            skArc(sketch, "E50.41.0.1", {"start": v(635.08, 29.21) * mm, "mid": v(633.14, 26.38) * mm, "end": v(632.46, 23.01) * mm});
            skArc(sketch, "E50.41.0.2", {"start": v(637.46, 29.21) * mm, "mid": v(639.4, 26.38) * mm, "end": v(640.08, 23.01) * mm});
            skLineSegment(sketch, "E50.41.0.3", {"start": v(640.08, 19.05) * mm, "end": v(640.08, 23.01) * mm});
            skLineSegment(sketch, "E50.41.0.4", {"start": v(632.46, 19.05) * mm, "end": v(632.46, 23.01) * mm});
            skLineSegment(sketch, "E50.41.0.5", {"start": v(640.08, 19.05) * mm, "end": v(632.46, 19.05) * mm});
            skLineSegment(sketch, "E50.42.0.0", {"start": v(652.7, 29.21) * mm, "end": v(650.32, 29.21) * mm});
            skArc(sketch, "E50.42.0.1", {"start": v(650.32, 29.21) * mm, "mid": v(648.38, 26.38) * mm, "end": v(647.7, 23.01) * mm});
            skArc(sketch, "E50.42.0.2", {"start": v(652.7, 29.21) * mm, "mid": v(654.64, 26.38) * mm, "end": v(655.32, 23.01) * mm});
            skLineSegment(sketch, "E50.42.0.3", {"start": v(655.32, 19.05) * mm, "end": v(655.32, 23.01) * mm});
            skLineSegment(sketch, "E50.42.0.4", {"start": v(647.7, 19.05) * mm, "end": v(647.7, 23.01) * mm});
            skLineSegment(sketch, "E50.42.0.5", {"start": v(655.32, 19.05) * mm, "end": v(647.7, 19.05) * mm});
            skLineSegment(sketch, "E50.43.0.0", {"start": v(667.94, 29.21) * mm, "end": v(665.56, 29.21) * mm});
            skArc(sketch, "E50.43.0.1", {"start": v(665.56, 29.21) * mm, "mid": v(663.62, 26.38) * mm, "end": v(662.94, 23.01) * mm});
            skArc(sketch, "E50.43.0.2", {"start": v(667.94, 29.21) * mm, "mid": v(669.88, 26.38) * mm, "end": v(670.56, 23.01) * mm});
            skLineSegment(sketch, "E50.43.0.3", {"start": v(670.56, 19.05) * mm, "end": v(670.56, 23.01) * mm});
            skLineSegment(sketch, "E50.43.0.4", {"start": v(662.94, 19.05) * mm, "end": v(662.94, 23.01) * mm});
            skLineSegment(sketch, "E50.43.0.5", {"start": v(670.56, 19.05) * mm, "end": v(662.94, 19.05) * mm});
            skLineSegment(sketch, "E50.44.0.0", {"start": v(683.18, 29.21) * mm, "end": v(680.8, 29.21) * mm});
            skArc(sketch, "E50.44.0.1", {"start": v(680.8, 29.21) * mm, "mid": v(678.86, 26.38) * mm, "end": v(678.18, 23.01) * mm});
            skArc(sketch, "E50.44.0.2", {"start": v(683.18, 29.21) * mm, "mid": v(685.12, 26.38) * mm, "end": v(685.8, 23.01) * mm});
            skLineSegment(sketch, "E50.44.0.3", {"start": v(685.8, 19.05) * mm, "end": v(685.8, 23.01) * mm});
            skLineSegment(sketch, "E50.44.0.4", {"start": v(678.18, 19.05) * mm, "end": v(678.18, 23.01) * mm});
            skLineSegment(sketch, "E50.44.0.5", {"start": v(685.8, 19.05) * mm, "end": v(678.18, 19.05) * mm});
            skLineSegment(sketch, "E50.45.0.0", {"start": v(698.42, 29.21) * mm, "end": v(696.04, 29.21) * mm});
            skArc(sketch, "E50.45.0.1", {"start": v(696.04, 29.21) * mm, "mid": v(694.1, 26.38) * mm, "end": v(693.42, 23.01) * mm});
            skArc(sketch, "E50.45.0.2", {"start": v(698.42, 29.21) * mm, "mid": v(700.36, 26.38) * mm, "end": v(701.04, 23.01) * mm});
            skLineSegment(sketch, "E50.45.0.3", {"start": v(701.04, 19.05) * mm, "end": v(701.04, 23.01) * mm});
            skLineSegment(sketch, "E50.45.0.4", {"start": v(693.42, 19.05) * mm, "end": v(693.42, 23.01) * mm});
            skLineSegment(sketch, "E50.45.0.5", {"start": v(701.04, 19.05) * mm, "end": v(693.42, 19.05) * mm});
            skLineSegment(sketch, "E50.46.0.0", {"start": v(713.66, 29.21) * mm, "end": v(711.28, 29.21) * mm});
            skArc(sketch, "E50.46.0.1", {"start": v(711.28, 29.21) * mm, "mid": v(709.34, 26.38) * mm, "end": v(708.66, 23.01) * mm});
            skArc(sketch, "E50.46.0.2", {"start": v(713.66, 29.21) * mm, "mid": v(715.6, 26.38) * mm, "end": v(716.28, 23.01) * mm});
            skLineSegment(sketch, "E50.46.0.3", {"start": v(716.28, 19.05) * mm, "end": v(716.28, 23.01) * mm});
            skLineSegment(sketch, "E50.46.0.4", {"start": v(708.66, 19.05) * mm, "end": v(708.66, 23.01) * mm});
            skLineSegment(sketch, "E50.46.0.5", {"start": v(716.28, 19.05) * mm, "end": v(708.66, 19.05) * mm});
            skLineSegment(sketch, "E50.47.0.0", {"start": v(728.9, 29.21) * mm, "end": v(726.52, 29.21) * mm});
            skArc(sketch, "E50.47.0.1", {"start": v(726.52, 29.21) * mm, "mid": v(724.58, 26.38) * mm, "end": v(723.9, 23.01) * mm});
            skArc(sketch, "E50.47.0.2", {"start": v(728.9, 29.21) * mm, "mid": v(730.84, 26.38) * mm, "end": v(731.52, 23.01) * mm});
            skLineSegment(sketch, "E50.47.0.3", {"start": v(731.52, 19.05) * mm, "end": v(731.52, 23.01) * mm});
            skLineSegment(sketch, "E50.47.0.4", {"start": v(723.9, 19.05) * mm, "end": v(723.9, 23.01) * mm});
            skLineSegment(sketch, "E50.47.0.5", {"start": v(731.52, 19.05) * mm, "end": v(723.9, 19.05) * mm});
            skLineSegment(sketch, "E50.48.0.0", {"start": v(744.14, 29.21) * mm, "end": v(741.76, 29.21) * mm});
            skArc(sketch, "E50.48.0.1", {"start": v(741.76, 29.21) * mm, "mid": v(739.82, 26.38) * mm, "end": v(739.14, 23.01) * mm});
            skArc(sketch, "E50.48.0.2", {"start": v(744.14, 29.21) * mm, "mid": v(746.08, 26.38) * mm, "end": v(746.76, 23.01) * mm});
            skLineSegment(sketch, "E50.48.0.3", {"start": v(746.76, 19.05) * mm, "end": v(746.76, 23.01) * mm});
            skLineSegment(sketch, "E50.48.0.4", {"start": v(739.14, 19.05) * mm, "end": v(739.14, 23.01) * mm});
            skLineSegment(sketch, "E50.48.0.5", {"start": v(746.76, 19.05) * mm, "end": v(739.14, 19.05) * mm});
            skLineSegment(sketch, "E50.49.0.0", {"start": v(759.38, 29.21) * mm, "end": v(757, 29.21) * mm});
            skArc(sketch, "E50.49.0.1", {"start": v(757, 29.21) * mm, "mid": v(755.06, 26.38) * mm, "end": v(754.38, 23.01) * mm});
            skArc(sketch, "E50.49.0.2", {"start": v(759.38, 29.21) * mm, "mid": v(761.32, 26.38) * mm, "end": v(762, 23.01) * mm});
            skLineSegment(sketch, "E50.49.0.3", {"start": v(762, 19.05) * mm, "end": v(762, 23.01) * mm});
            skLineSegment(sketch, "E50.49.0.4", {"start": v(754.38, 19.05) * mm, "end": v(754.38, 23.01) * mm});
            skLineSegment(sketch, "E50.49.0.5", {"start": v(762, 19.05) * mm, "end": v(754.38, 19.05) * mm});
            skLineSegment(sketch, "E50.direction1", {"start": v(10.24, 29.21) * mm, "end": v(25.48, 29.21) * mm, "construction": true});
            skSolve(sketch);
        }
        {
            var Q0;
            Q0=qSketchRegion(id+"F8",true);
            extrude(context, id + "F9", {"entities" : qUnion([Q0]), "operationType" : NewBodyOperationType.ADD, "oppositeDirection" : true, "depth" : 127 * mm});
        }
        {
            var Q0;
            {var subQ7=makeQuery(id+"F1.opExtrude","CAP_EDGE",EDGE,{"disambiguationData":[OSD([sQuery(id+"F0.wireOp",EDGE,"E0")])],"isStart":false});Q0=makeQuery(id+"F2.imprint","IMPRINT",FACE,{"disambiguationData":[TD([[makeQuery(id+"F2.imprint","IMPRINT",EDGE,{"derivedFrom":subQ7}),1.0]])]});}
            var sketch = newSketch(context, id + "F10", { "sketchPlane" : qUnion([Q0])});
            skLineSegment(sketch, "E51", {"start": v(0, 0) * mm, "end": v(31.75, 0) * mm});
            skLineSegment(sketch, "E52", {"start": v(31.75, 0) * mm, "end": v(31.75, 25.53) * mm});
            skLineSegment(sketch, "E53", {"start": v(31.75, 25.53) * mm, "end": v(50.8, 25.53) * mm});
            skLineSegment(sketch, "E54.MirrorCS", {"start": v(31.75, 25.53) * mm, "end": v(12.7, 25.53) * mm});
            skCircle(sketch, "E55", {"center": v(12.7, 25.53) * mm, "radius": 4.37 * mm});
            skCircle(sketch, "E56", {"center": v(50.8, 25.53) * mm, "radius": 4.37 * mm});
            skLineSegment(sketch, "E57", {"start": v(0, 0) * mm, "end": v(0, 114.3) * mm});
            skLineSegment(sketch, "E58", {"start": v(0, 114.3) * mm, "end": v(170.29, 114.3) * mm});
            skCircle(sketch, "E59.MirrorC", {"center": v(12.7, 203.07) * mm, "radius": 4.37 * mm});
            skCircle(sketch, "E60.MirrorC", {"center": v(50.8, 203.07) * mm, "radius": 4.37 * mm});
            skLineSegment(sketch, "E61", {"start": v(0, 0) * mm, "end": v(381, 0) * mm});
            skPoint(sketch, "E61.endSnap0", {"position": v(15.88, 0) * mm});
            skLineSegment(sketch, "E62", {"start": v(381, 0) * mm, "end": v(381, 236.8) * mm});
            skCircle(sketch, "E63.MirrorC", {"center": v(711.2, 203.07) * mm, "radius": 4.37 * mm});
            skCircle(sketch, "E64.MirrorC", {"center": v(749.3, 203.07) * mm, "radius": 4.37 * mm});
            skCircle(sketch, "E65.MirrorC", {"center": v(711.2, 25.53) * mm, "radius": 4.37 * mm});
            skCircle(sketch, "E66.MirrorC", {"center": v(749.3, 25.53) * mm, "radius": 4.37 * mm});
            skSolve(sketch);
        }
        {
            var Q0;
            Q0=sQuery(id+"F10.wireOp",VERTEX,"E59.MirrorC.center");
            var Q1;
            Q1=sQuery(id+"F10.wireOp",VERTEX,"E60.MirrorC.center");
            var Q2;
            Q2=sQuery(id+"F10.wireOp",VERTEX,"E55.center");
            var Q3;
            Q3=sQuery(id+"F10.wireOp",VERTEX,"E53.end");
            var Q4;
            Q4=sQuery(id+"F10.wireOp",VERTEX,"E63.MirrorC.center");
            var Q5;
            Q5=sQuery(id+"F10.wireOp",VERTEX,"E64.MirrorC.center");
            var Q6;
            Q6=sQuery(id+"F10.wireOp",VERTEX,"E66.MirrorC.center");
            var Q7;
            Q7=sQuery(id+"F10.wireOp",VERTEX,"E65.MirrorC.center");
            var Q8;
            Q8=makeQuery(id+"F1.opExtrude","SWEPT_BODY",BODY,{"disambiguationData":[OSD([sQuery(id+"F0.wireOp",EDGE,"E0"),sQuery(id+"F0.wireOp",EDGE,"E1.0"),sQuery(id+"F0.wireOp",EDGE,"E2"),sQuery(id+"F0.wireOp",EDGE,"E3"),sQuery(id+"F0.wireOp",EDGE,"E4.0"),sQuery(id+"F0.wireOp",EDGE,"E5.0"),sQuery(id+"F0.wireOp",EDGE,"E6.0"),sQuery(id+"F0.wireOp",EDGE,"E7.0"),sQuery(id+"F0.wireOp",EDGE,"E8.trimOffspring"),sQuery(id+"F0.wireOp",EDGE,"E9.trimOffspring"),sQuery(id+"F0.wireOp",EDGE,"E10.trimOffspring"),sQuery(id+"F0.wireOp",EDGE,"E11.trimOffspring")])]});
            hole(context, id + "F11", {"style" : HoleStyle.SIMPLE, "endStyle" : HoleEndStyle.THROUGH, "holeDiameter" : 8.74 * mm, "tappedDepth" : 12.7 * mm, "tapClearance" : 3, "locations" : qUnion([Q0, Q1, Q2, Q3, Q4, Q5, Q6, Q7]), "scope" : qUnion([Q8])});
        }
    });
